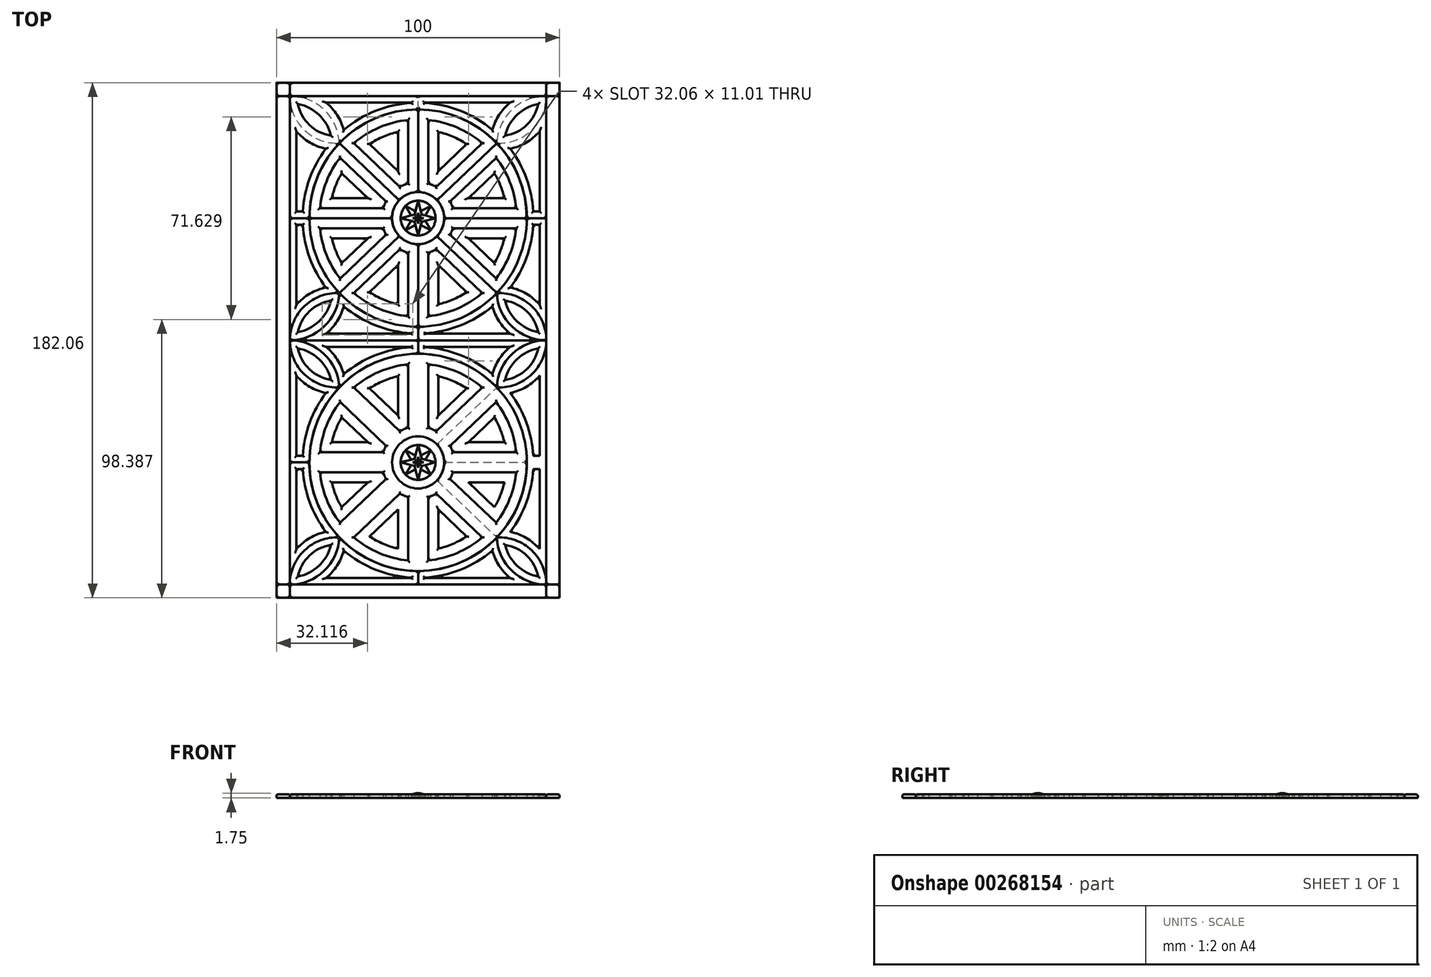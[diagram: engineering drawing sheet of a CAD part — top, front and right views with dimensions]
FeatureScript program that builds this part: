
annotation { "Feature Type Name" : "Feature", "Feature Type Description" : "" }
export const myFeature = defineFeature(function(context is Context, id is Id, definition is map)
    precondition{}
    {
        {
            var Q0;
            Q0=qCreatedBy(makeId("Top.planeOp"),FACE);
            var sketch = newSketch(context, id + "F0", { "sketchPlane" : qUnion([Q0])});
            skLineSegment(sketch, "E0", {"start": v(-100, 182.06) * mm, "end": v(-95.31, 182.06) * mm});
            skLineSegment(sketch, "E1", {"start": v(0, 182.06) * mm, "end": v(-4.69, 182.06) * mm});
            skLineSegment(sketch, "E2", {"start": v(0, 0) * mm, "end": v(-4.69, 0) * mm});
            skLineSegment(sketch, "E3", {"start": v(-100, 0) * mm, "end": v(-95.31, 0) * mm});
            skLineSegment(sketch, "E4", {"start": v(-100, 182.06) * mm, "end": v(-100, 177.37) * mm});
            skLineSegment(sketch, "E5", {"start": v(-100, 0) * mm, "end": v(-100, 4.69) * mm});
            skLineSegment(sketch, "E6", {"start": v(-95.31, 91.03) * mm, "end": v(-4.69, 91.03) * mm});
            skLineSegment(sketch, "E7", {"start": v(-56.66, 127.86) * mm, "end": v(-77.8, 107.7) * mm});
            skLineSegment(sketch, "E8", {"start": v(-56.66, 140.55) * mm, "end": v(-77.8, 160.7) * mm});
            skLineSegment(sketch, "E9", {"start": v(-50, 143.4) * mm, "end": v(-50, 172.61) * mm});
            skLineSegment(sketch, "E10", {"start": v(-50, 125) * mm, "end": v(-50, 95.8) * mm});
            skLineSegment(sketch, "E11", {"start": v(-40.8, 134.2) * mm, "end": v(-11.59, 134.2) * mm});
            skLineSegment(sketch, "E12", {"start": v(-59.2, 134.2) * mm, "end": v(-88.41, 134.2) * mm});
            skLineSegment(sketch, "E13", {"start": v(-43.34, 140.55) * mm, "end": v(-22.2, 160.7) * mm});
            skLineSegment(sketch, "E14", {"start": v(-43.34, 127.86) * mm, "end": v(-22.2, 107.7) * mm});
            skCircle(sketch, "E15.0", {"center": v(-50, 134.2) * mm, "radius": 6.15 * mm});
            skLineSegment(sketch, "E16", {"start": v(-11.59, 134.2) * mm, "end": v(-4.69, 134.2) * mm});
            skLineSegment(sketch, "E17", {"start": v(-88.41, 134.2) * mm, "end": v(-95.31, 134.2) * mm});
            skLineSegment(sketch, "E18", {"start": v(-50, 172.61) * mm, "end": v(-50, 177.37) * mm});
            skLineSegment(sketch, "E19", {"start": v(-50, 95.8) * mm, "end": v(-50, 91.03) * mm});
            skLineSegment(sketch, "E20", {"start": v(-56.15, 134.2) * mm, "end": v(-51.27, 135.47) * mm});
            skLineSegment(sketch, "E21", {"start": v(-50, 140.35) * mm, "end": v(-51.27, 135.47) * mm});
            skLineSegment(sketch, "E22", {"start": v(-50, 140.35) * mm, "end": v(-48.73, 135.46) * mm});
            skLineSegment(sketch, "E23", {"start": v(-43.85, 134.2) * mm, "end": v(-48.73, 135.46) * mm});
            skLineSegment(sketch, "E24", {"start": v(-43.85, 134.2) * mm, "end": v(-48.73, 132.93) * mm});
            skLineSegment(sketch, "E25", {"start": v(-50, 128.05) * mm, "end": v(-48.73, 132.93) * mm});
            skLineSegment(sketch, "E26", {"start": v(-50, 128.05) * mm, "end": v(-51.27, 132.93) * mm});
            skLineSegment(sketch, "E27", {"start": v(-56.15, 134.2) * mm, "end": v(-51.27, 132.93) * mm});
            skLineSegment(sketch, "E28", {"start": v(-45.55, 138.45) * mm, "end": v(-47.46, 135.13) * mm});
            skLineSegment(sketch, "E29", {"start": v(-45.55, 138.45) * mm, "end": v(-49.03, 136.63) * mm});
            skLineSegment(sketch, "E30", {"start": v(-54.45, 138.45) * mm, "end": v(-52.55, 135.14) * mm});
            skLineSegment(sketch, "E31", {"start": v(-54.45, 138.45) * mm, "end": v(-50.97, 136.63) * mm});
            skLineSegment(sketch, "E32", {"start": v(-54.45, 129.96) * mm, "end": v(-52.55, 133.26) * mm});
            skLineSegment(sketch, "E33", {"start": v(-54.45, 129.96) * mm, "end": v(-50.97, 131.77) * mm});
            skLineSegment(sketch, "E34", {"start": v(-45.55, 129.96) * mm, "end": v(-49.03, 131.77) * mm});
            skLineSegment(sketch, "E35", {"start": v(-45.55, 129.96) * mm, "end": v(-47.46, 133.26) * mm});
            skLineSegment(sketch, "E36.0", {"start": v(-50, 136.11) * mm, "end": v(-49.6, 134.59) * mm});
            skLineSegment(sketch, "E36.1", {"start": v(-48.1, 134.2) * mm, "end": v(-49.6, 134.59) * mm});
            skLineSegment(sketch, "E36.2", {"start": v(-50, 136.11) * mm, "end": v(-50.4, 134.6) * mm});
            skLineSegment(sketch, "E36.3", {"start": v(-48.1, 134.2) * mm, "end": v(-49.6, 133.8) * mm});
            skLineSegment(sketch, "E36.4", {"start": v(-51.91, 134.2) * mm, "end": v(-50.4, 134.6) * mm});
            skLineSegment(sketch, "E36.5", {"start": v(-51.91, 134.2) * mm, "end": v(-50.4, 133.8) * mm});
            skLineSegment(sketch, "E36.6", {"start": v(-50, 132.29) * mm, "end": v(-50.4, 133.8) * mm});
            skLineSegment(sketch, "E36.7", {"start": v(-50, 132.29) * mm, "end": v(-49.6, 133.8) * mm});
            skLineSegment(sketch, "E37", {"start": v(-95.31, 4.69) * mm, "end": v(-100, 4.69) * mm});
            skLineSegment(sketch, "E38", {"start": v(-95.31, 4.69) * mm, "end": v(-95.31, 0) * mm});
            skLineSegment(sketch, "E39", {"start": v(-95.31, 0) * mm, "end": v(-100, 0) * mm});
            skLineSegment(sketch, "E40", {"start": v(-100, 4.69) * mm, "end": v(-100, 0) * mm});
            skLineSegment(sketch, "E41", {"start": v(-4.69, 4.69) * mm, "end": v(0, 4.69) * mm});
            skLineSegment(sketch, "E42", {"start": v(0, 0) * mm, "end": v(0, 4.69) * mm});
            skLineSegment(sketch, "E43", {"start": v(-4.69, 0) * mm, "end": v(-4.69, 4.69) * mm});
            skLineSegment(sketch, "E44", {"start": v(-95.31, 0) * mm, "end": v(-4.69, 0) * mm});
            skLineSegment(sketch, "E45", {"start": v(-95.31, 4.69) * mm, "end": v(-4.69, 4.69) * mm});
            skLineSegment(sketch, "E46", {"start": v(-95.31, 177.37) * mm, "end": v(-100, 177.37) * mm});
            skLineSegment(sketch, "E47", {"start": v(-100, 177.37) * mm, "end": v(-100, 182.06) * mm});
            skLineSegment(sketch, "E48", {"start": v(-95.31, 182.06) * mm, "end": v(-95.31, 177.37) * mm});
            skLineSegment(sketch, "E49", {"start": v(-4.69, 177.37) * mm, "end": v(-4.69, 182.06) * mm});
            skLineSegment(sketch, "E50", {"start": v(0, 182.06) * mm, "end": v(0, 177.37) * mm});
            skLineSegment(sketch, "E51", {"start": v(0, 177.37) * mm, "end": v(-4.69, 177.37) * mm});
            skLineSegment(sketch, "E52", {"start": v(-100, 177.37) * mm, "end": v(-100, 4.69) * mm});
            skLineSegment(sketch, "E53", {"start": v(-4.69, 4.69) * mm, "end": v(-4.69, 177.37) * mm});
            skLineSegment(sketch, "E54", {"start": v(0, 4.69) * mm, "end": v(0, 177.37) * mm});
            skLineSegment(sketch, "E55", {"start": v(-4.69, 182.06) * mm, "end": v(-95.31, 182.06) * mm});
            skArc(sketch, "E56", {"start": v(-43.34, 127.86) * mm, "mid": v(-41.46, 130.78) * mm, "end": v(-40.8, 134.2) * mm});
            skArc(sketch, "E57", {"start": v(-50, 125) * mm, "mid": v(-46.38, 125.74) * mm, "end": v(-43.34, 127.86) * mm});
            skArc(sketch, "E58", {"start": v(-56.66, 127.86) * mm, "mid": v(-53.62, 125.74) * mm, "end": v(-50, 125) * mm});
            skArc(sketch, "E59", {"start": v(-59.2, 134.2) * mm, "mid": v(-58.54, 130.78) * mm, "end": v(-56.66, 127.86) * mm});
            skArc(sketch, "E60", {"start": v(-56.66, 140.55) * mm, "mid": v(-58.54, 137.62) * mm, "end": v(-59.2, 134.2) * mm});
            skArc(sketch, "E61", {"start": v(-50, 143.4) * mm, "mid": v(-53.62, 142.66) * mm, "end": v(-56.66, 140.55) * mm});
            skArc(sketch, "E62", {"start": v(-43.34, 140.55) * mm, "mid": v(-46.38, 142.66) * mm, "end": v(-50, 143.4) * mm});
            skArc(sketch, "E63", {"start": v(-40.8, 134.2) * mm, "mid": v(-41.46, 137.62) * mm, "end": v(-43.34, 140.55) * mm});
            skArc(sketch, "E64", {"start": v(-50, 95.8) * mm, "mid": v(-34.87, 98.9) * mm, "end": v(-22.2, 107.7) * mm});
            skArc(sketch, "E65", {"start": v(-77.8, 107.7) * mm, "mid": v(-65.13, 98.9) * mm, "end": v(-50, 95.8) * mm});
            skArc(sketch, "E66", {"start": v(-88.41, 134.2) * mm, "mid": v(-85.66, 119.93) * mm, "end": v(-77.8, 107.7) * mm});
            skArc(sketch, "E67", {"start": v(-77.8, 160.7) * mm, "mid": v(-85.66, 148.47) * mm, "end": v(-88.41, 134.2) * mm});
            skArc(sketch, "E68", {"start": v(-50, 172.61) * mm, "mid": v(-65.13, 169.5) * mm, "end": v(-77.8, 160.7) * mm});
            skArc(sketch, "E69", {"start": v(-22.2, 160.7) * mm, "mid": v(-34.87, 169.5) * mm, "end": v(-50, 172.61) * mm});
            skArc(sketch, "E70", {"start": v(-11.59, 134.2) * mm, "mid": v(-14.34, 148.47) * mm, "end": v(-22.2, 160.7) * mm});
            skArc(sketch, "E71", {"start": v(-22.2, 107.7) * mm, "mid": v(-14.34, 119.93) * mm, "end": v(-11.59, 134.2) * mm});
            skLineSegment(sketch, "E72.0", {"start": v(-56.42, 145.23) * mm, "end": v(-72.65, 160.7) * mm});
            skArc(sketch, "E72.1", {"start": v(-53.56, 146.45) * mm, "mid": v(-55.02, 145.93) * mm, "end": v(-56.42, 145.23) * mm});
            skLineSegment(sketch, "E72.2", {"start": v(-53.56, 146.45) * mm, "end": v(-53.56, 168.87) * mm});
            skArc(sketch, "E72.3", {"start": v(-53.56, 168.87) * mm, "mid": v(-63.73, 166.24) * mm, "end": v(-72.65, 160.7) * mm});
            skLineSegment(sketch, "E73.0", {"start": v(-57.11, 150.8) * mm, "end": v(-67.16, 160.38) * mm});
            skLineSegment(sketch, "E73.1", {"start": v(-57.11, 150.8) * mm, "end": v(-57.11, 164.68) * mm});
            skArc(sketch, "E73.2", {"start": v(-57.11, 164.68) * mm, "mid": v(-62.33, 162.97) * mm, "end": v(-67.16, 160.38) * mm});
            skArc(sketch, "E74.0", {"start": v(-77.56, 155.54) * mm, "mid": v(-82.36, 147.15) * mm, "end": v(-84.67, 137.76) * mm});
            skLineSegment(sketch, "E74.1", {"start": v(-61.32, 140.08) * mm, "end": v(-77.56, 155.54) * mm});
            skArc(sketch, "E74.2", {"start": v(-61.32, 140.08) * mm, "mid": v(-61.84, 138.94) * mm, "end": v(-62.25, 137.76) * mm});
            skLineSegment(sketch, "E74.3", {"start": v(-62.25, 137.76) * mm, "end": v(-84.67, 137.76) * mm});
            skArc(sketch, "E75.0", {"start": v(-76.97, 150.08) * mm, "mid": v(-79.06, 145.83) * mm, "end": v(-80.48, 141.31) * mm});
            skLineSegment(sketch, "E75.1", {"start": v(-67.78, 141.31) * mm, "end": v(-76.97, 150.08) * mm});
            skLineSegment(sketch, "E75.2", {"start": v(-67.78, 141.31) * mm, "end": v(-80.48, 141.31) * mm});
            skArc(sketch, "E76.0", {"start": v(-84.67, 130.65) * mm, "mid": v(-82.36, 121.25) * mm, "end": v(-77.56, 112.86) * mm});
            skLineSegment(sketch, "E76.1", {"start": v(-62.25, 130.65) * mm, "end": v(-84.67, 130.65) * mm});
            skArc(sketch, "E76.2", {"start": v(-62.25, 130.65) * mm, "mid": v(-61.84, 129.46) * mm, "end": v(-61.32, 128.33) * mm});
            skLineSegment(sketch, "E76.3", {"start": v(-61.32, 128.33) * mm, "end": v(-77.56, 112.86) * mm});
            skArc(sketch, "E77.0", {"start": v(-80.48, 127.09) * mm, "mid": v(-79.06, 122.57) * mm, "end": v(-76.97, 118.33) * mm});
            skLineSegment(sketch, "E77.1", {"start": v(-67.78, 127.09) * mm, "end": v(-80.48, 127.09) * mm});
            skLineSegment(sketch, "E77.2", {"start": v(-67.78, 127.09) * mm, "end": v(-76.97, 118.33) * mm});
            skArc(sketch, "E78.0", {"start": v(-72.65, 107.71) * mm, "mid": v(-63.73, 102.16) * mm, "end": v(-53.56, 99.53) * mm});
            skLineSegment(sketch, "E78.1", {"start": v(-56.42, 123.18) * mm, "end": v(-72.65, 107.71) * mm});
            skArc(sketch, "E78.2", {"start": v(-56.42, 123.18) * mm, "mid": v(-55.02, 122.48) * mm, "end": v(-53.56, 121.95) * mm});
            skLineSegment(sketch, "E78.3", {"start": v(-53.56, 121.95) * mm, "end": v(-53.56, 99.53) * mm});
            skArc(sketch, "E79.0", {"start": v(-67.16, 108.03) * mm, "mid": v(-62.33, 105.43) * mm, "end": v(-57.11, 103.72) * mm});
            skLineSegment(sketch, "E79.1", {"start": v(-57.11, 117.6) * mm, "end": v(-67.16, 108.03) * mm});
            skLineSegment(sketch, "E79.2", {"start": v(-57.11, 117.6) * mm, "end": v(-57.11, 103.72) * mm});
            skArc(sketch, "E80.0", {"start": v(-46.44, 99.53) * mm, "mid": v(-36.27, 102.16) * mm, "end": v(-27.35, 107.71) * mm});
            skLineSegment(sketch, "E80.1", {"start": v(-46.44, 121.95) * mm, "end": v(-46.44, 99.53) * mm});
            skArc(sketch, "E80.2", {"start": v(-46.44, 121.95) * mm, "mid": v(-44.98, 122.48) * mm, "end": v(-43.58, 123.18) * mm});
            skLineSegment(sketch, "E80.3", {"start": v(-43.58, 123.18) * mm, "end": v(-27.35, 107.71) * mm});
            skArc(sketch, "E81.0", {"start": v(-42.89, 103.72) * mm, "mid": v(-37.67, 105.43) * mm, "end": v(-32.84, 108.03) * mm});
            skLineSegment(sketch, "E81.1", {"start": v(-42.89, 117.6) * mm, "end": v(-42.89, 103.72) * mm});
            skLineSegment(sketch, "E81.2", {"start": v(-42.89, 117.6) * mm, "end": v(-32.84, 108.03) * mm});
            skArc(sketch, "E82.0", {"start": v(-27.35, 160.7) * mm, "mid": v(-36.27, 166.24) * mm, "end": v(-46.44, 168.87) * mm});
            skLineSegment(sketch, "E82.1", {"start": v(-43.58, 145.23) * mm, "end": v(-27.35, 160.7) * mm});
            skArc(sketch, "E82.2", {"start": v(-43.58, 145.23) * mm, "mid": v(-44.98, 145.93) * mm, "end": v(-46.44, 146.45) * mm});
            skLineSegment(sketch, "E82.3", {"start": v(-46.44, 146.45) * mm, "end": v(-46.44, 168.87) * mm});
            skLineSegment(sketch, "E83.0", {"start": v(-42.89, 150.8) * mm, "end": v(-32.84, 160.38) * mm});
            skLineSegment(sketch, "E83.1", {"start": v(-42.89, 150.8) * mm, "end": v(-42.89, 164.68) * mm});
            skArc(sketch, "E83.2", {"start": v(-32.84, 160.38) * mm, "mid": v(-37.67, 162.97) * mm, "end": v(-42.89, 164.68) * mm});
            skArc(sketch, "E84.0", {"start": v(-15.33, 137.76) * mm, "mid": v(-17.64, 147.15) * mm, "end": v(-22.44, 155.54) * mm});
            skLineSegment(sketch, "E84.1", {"start": v(-37.75, 137.76) * mm, "end": v(-15.33, 137.76) * mm});
            skArc(sketch, "E84.2", {"start": v(-37.75, 137.76) * mm, "mid": v(-38.16, 138.94) * mm, "end": v(-38.68, 140.08) * mm});
            skLineSegment(sketch, "E84.3", {"start": v(-38.68, 140.08) * mm, "end": v(-22.44, 155.54) * mm});
            skLineSegment(sketch, "E85.0", {"start": v(-32.22, 141.31) * mm, "end": v(-23.03, 150.08) * mm});
            skLineSegment(sketch, "E85.1", {"start": v(-32.22, 141.31) * mm, "end": v(-19.52, 141.31) * mm});
            skArc(sketch, "E85.2", {"start": v(-19.52, 141.31) * mm, "mid": v(-20.94, 145.83) * mm, "end": v(-23.03, 150.08) * mm});
            skArc(sketch, "E86.0", {"start": v(-22.44, 112.86) * mm, "mid": v(-17.64, 121.25) * mm, "end": v(-15.33, 130.65) * mm});
            skLineSegment(sketch, "E86.1", {"start": v(-38.68, 128.33) * mm, "end": v(-22.44, 112.86) * mm});
            skArc(sketch, "E86.2", {"start": v(-38.68, 128.33) * mm, "mid": v(-38.16, 129.46) * mm, "end": v(-37.75, 130.65) * mm});
            skLineSegment(sketch, "E86.3", {"start": v(-37.75, 130.65) * mm, "end": v(-15.33, 130.65) * mm});
            skArc(sketch, "E87.0", {"start": v(-23.03, 118.33) * mm, "mid": v(-20.94, 122.57) * mm, "end": v(-19.52, 127.09) * mm});
            skLineSegment(sketch, "E87.1", {"start": v(-32.22, 127.09) * mm, "end": v(-23.03, 118.33) * mm});
            skLineSegment(sketch, "E87.2", {"start": v(-32.22, 127.09) * mm, "end": v(-19.52, 127.09) * mm});
            skLineSegment(sketch, "E88.MirrorCS", {"start": v(-48.1, 47.86) * mm, "end": v(-49.6, 47.47) * mm});
            skLineSegment(sketch, "E89.MirrorCS", {"start": v(-50, 49.77) * mm, "end": v(-50.4, 48.25) * mm});
            skLineSegment(sketch, "E90.MirrorCS", {"start": v(-51.91, 47.86) * mm, "end": v(-50.4, 48.25) * mm});
            skLineSegment(sketch, "E91.MirrorCS", {"start": v(-48.1, 47.86) * mm, "end": v(-49.6, 48.25) * mm});
            skLineSegment(sketch, "E92.MirrorCS", {"start": v(-50, 45.95) * mm, "end": v(-50.4, 47.46) * mm});
            skLineSegment(sketch, "E93.MirrorCS", {"start": v(-50, 45.95) * mm, "end": v(-49.6, 47.47) * mm});
            skLineSegment(sketch, "E94.MirrorCS", {"start": v(-50, 49.77) * mm, "end": v(-49.6, 48.25) * mm});
            skLineSegment(sketch, "E95.MirrorCS", {"start": v(-51.91, 47.86) * mm, "end": v(-50.4, 47.46) * mm});
            skLineSegment(sketch, "E96.MirrorCS", {"start": v(-56.15, 47.86) * mm, "end": v(-51.27, 46.59) * mm});
            skLineSegment(sketch, "E97.MirrorCS", {"start": v(-50, 86.27) * mm, "end": v(-50, 91.03) * mm});
            skLineSegment(sketch, "E98.MirrorCS", {"start": v(-50, 9.45) * mm, "end": v(-50, 4.69) * mm});
            skLineSegment(sketch, "E99.MirrorCS", {"start": v(-56.15, 47.86) * mm, "end": v(-51.27, 49.13) * mm});
            skLineSegment(sketch, "E100.MirrorCS", {"start": v(-50, 41.7) * mm, "end": v(-51.27, 46.59) * mm});
            skLineSegment(sketch, "E101.MirrorCS", {"start": v(-43.85, 47.86) * mm, "end": v(-48.73, 46.6) * mm});
            skLineSegment(sketch, "E102.MirrorCS", {"start": v(-54.45, 43.61) * mm, "end": v(-52.55, 46.92) * mm});
            skLineSegment(sketch, "E103.MirrorCS", {"start": v(-45.55, 43.61) * mm, "end": v(-47.46, 46.93) * mm});
            skLineSegment(sketch, "E104.MirrorCS", {"start": v(-50, 41.7) * mm, "end": v(-48.73, 46.6) * mm});
            skArc(sketch, "E105.MirrorCS", {"start": v(-43.34, 54.2) * mm, "mid": v(-41.46, 51.28) * mm, "end": v(-40.8, 47.86) * mm});
            skLineSegment(sketch, "E106.MirrorCS", {"start": v(-45.55, 52.1) * mm, "end": v(-47.46, 48.8) * mm});
            skLineSegment(sketch, "E107.MirrorCS", {"start": v(-45.55, 52.1) * mm, "end": v(-49.03, 50.3) * mm});
            skArc(sketch, "E108.MirrorCS", {"start": v(-56.66, 54.2) * mm, "mid": v(-53.62, 56.31) * mm, "end": v(-50, 57.06) * mm});
            skArc(sketch, "E109.MirrorCS", {"start": v(-56.66, 41.51) * mm, "mid": v(-58.54, 44.44) * mm, "end": v(-59.2, 47.86) * mm});
            skLineSegment(sketch, "E110.MirrorCS", {"start": v(-43.85, 47.86) * mm, "end": v(-48.73, 49.13) * mm});
            skLineSegment(sketch, "E111.MirrorCS", {"start": v(-50, 54.01) * mm, "end": v(-48.73, 49.13) * mm});
            skArc(sketch, "E112.MirrorCS", {"start": v(-40.8, 47.86) * mm, "mid": v(-41.46, 44.44) * mm, "end": v(-43.34, 41.51) * mm});
            skArc(sketch, "E113.MirrorCS", {"start": v(-50, 38.66) * mm, "mid": v(-53.62, 39.4) * mm, "end": v(-56.66, 41.51) * mm});
            skArc(sketch, "E114.MirrorCS", {"start": v(-59.2, 47.86) * mm, "mid": v(-58.54, 51.28) * mm, "end": v(-56.66, 54.2) * mm});
            skLineSegment(sketch, "E115.MirrorCS", {"start": v(-54.45, 43.61) * mm, "end": v(-50.97, 45.43) * mm});
            skLineSegment(sketch, "E116.MirrorCS", {"start": v(-54.45, 52.1) * mm, "end": v(-50.97, 50.3) * mm});
            skLineSegment(sketch, "E117.MirrorCS", {"start": v(-45.55, 43.61) * mm, "end": v(-49.03, 45.43) * mm});
            skLineSegment(sketch, "E118.MirrorCS", {"start": v(-50, 54.01) * mm, "end": v(-51.27, 49.13) * mm});
            skLineSegment(sketch, "E119.MirrorCS", {"start": v(-54.45, 52.1) * mm, "end": v(-52.55, 48.8) * mm});
            skArc(sketch, "E120.MirrorCS", {"start": v(-62.25, 51.41) * mm, "mid": v(-61.84, 52.6) * mm, "end": v(-61.32, 53.73) * mm});
            skArc(sketch, "E121.MirrorCS", {"start": v(-61.32, 41.98) * mm, "mid": v(-61.84, 43.12) * mm, "end": v(-62.25, 44.3) * mm});
            skCircle(sketch, "E122.MirrorC", {"center": v(-50, 47.86) * mm, "radius": 6.15 * mm});
            skArc(sketch, "E123.MirrorCS", {"start": v(-53.56, 35.6) * mm, "mid": v(-55.02, 36.13) * mm, "end": v(-56.42, 36.83) * mm});
            skArc(sketch, "E124.MirrorCS", {"start": v(-43.58, 36.83) * mm, "mid": v(-44.98, 36.13) * mm, "end": v(-46.44, 35.6) * mm});
            skArc(sketch, "E125.MirrorCS", {"start": v(-56.42, 58.88) * mm, "mid": v(-55.02, 59.58) * mm, "end": v(-53.56, 60.1) * mm});
            skArc(sketch, "E126.MirrorCS", {"start": v(-38.68, 53.73) * mm, "mid": v(-38.16, 52.6) * mm, "end": v(-37.75, 51.41) * mm});
            skArc(sketch, "E127.MirrorCS", {"start": v(-37.75, 44.3) * mm, "mid": v(-38.16, 43.12) * mm, "end": v(-38.68, 41.98) * mm});
            skArc(sketch, "E128.MirrorCS", {"start": v(-46.44, 60.1) * mm, "mid": v(-44.98, 59.58) * mm, "end": v(-43.58, 58.88) * mm});
            skArc(sketch, "E129.MirrorCS", {"start": v(-42.89, 78.34) * mm, "mid": v(-37.67, 76.63) * mm, "end": v(-32.84, 74.03) * mm});
            skArc(sketch, "E130.MirrorCS", {"start": v(-67.16, 74.03) * mm, "mid": v(-62.33, 76.63) * mm, "end": v(-57.11, 78.34) * mm});
            skLineSegment(sketch, "E131.MirrorCS", {"start": v(-32.22, 40.75) * mm, "end": v(-23.03, 31.98) * mm});
            skArc(sketch, "E132.MirrorCS", {"start": v(-23.03, 63.73) * mm, "mid": v(-20.94, 59.48) * mm, "end": v(-19.52, 54.97) * mm});
            skArc(sketch, "E133.MirrorCS", {"start": v(-76.97, 31.98) * mm, "mid": v(-79.06, 36.23) * mm, "end": v(-80.48, 40.75) * mm});
            skArc(sketch, "E134.MirrorCS", {"start": v(-80.48, 54.97) * mm, "mid": v(-79.06, 59.48) * mm, "end": v(-76.97, 63.73) * mm});
            skArc(sketch, "E135.MirrorCS", {"start": v(-19.52, 40.75) * mm, "mid": v(-20.94, 36.23) * mm, "end": v(-23.03, 31.98) * mm});
            skLineSegment(sketch, "E136.MirrorCS", {"start": v(-56.42, 36.83) * mm, "end": v(-72.65, 21.37) * mm});
            skArc(sketch, "E137.MirrorCS", {"start": v(-72.65, 74.35) * mm, "mid": v(-63.73, 79.9) * mm, "end": v(-53.56, 82.53) * mm});
            skLineSegment(sketch, "E138.MirrorCS", {"start": v(-32.22, 54.97) * mm, "end": v(-23.03, 63.73) * mm});
            skLineSegment(sketch, "E139.MirrorCS", {"start": v(-46.44, 35.6) * mm, "end": v(-46.44, 13.19) * mm});
            skLineSegment(sketch, "E140.MirrorCS", {"start": v(-62.25, 51.41) * mm, "end": v(-84.67, 51.41) * mm});
            skArc(sketch, "E141.MirrorCS", {"start": v(-22.2, 74.35) * mm, "mid": v(-14.34, 62.13) * mm, "end": v(-11.59, 47.86) * mm});
            skLineSegment(sketch, "E142.MirrorCS", {"start": v(-32.22, 40.75) * mm, "end": v(-19.52, 40.75) * mm});
            skLineSegment(sketch, "E143.MirrorCS", {"start": v(-43.58, 58.88) * mm, "end": v(-27.35, 74.35) * mm});
            skLineSegment(sketch, "E144.MirrorCS", {"start": v(-42.89, 31.26) * mm, "end": v(-42.89, 17.38) * mm});
            skArc(sketch, "E145.MirrorCS", {"start": v(-15.33, 44.3) * mm, "mid": v(-17.64, 34.91) * mm, "end": v(-22.44, 26.52) * mm});
            skLineSegment(sketch, "E146.MirrorCS", {"start": v(-57.11, 64.46) * mm, "end": v(-67.16, 74.03) * mm});
            skLineSegment(sketch, "E147.MirrorCS", {"start": v(-61.32, 41.98) * mm, "end": v(-77.56, 26.52) * mm});
            skArc(sketch, "E148.MirrorCS", {"start": v(-50, 86.27) * mm, "mid": v(-34.87, 83.16) * mm, "end": v(-22.2, 74.35) * mm});
            skLineSegment(sketch, "E149.MirrorCS", {"start": v(-53.56, 35.6) * mm, "end": v(-53.56, 13.19) * mm});
            skLineSegment(sketch, "E150.MirrorCS", {"start": v(-38.68, 53.73) * mm, "end": v(-22.44, 69.2) * mm});
            skArc(sketch, "E151.MirrorCS", {"start": v(-43.34, 41.51) * mm, "mid": v(-46.38, 39.4) * mm, "end": v(-50, 38.66) * mm});
            skLineSegment(sketch, "E152.MirrorCS", {"start": v(-56.42, 58.88) * mm, "end": v(-72.65, 74.35) * mm});
            skArc(sketch, "E153.MirrorCS", {"start": v(-77.8, 74.35) * mm, "mid": v(-65.13, 83.16) * mm, "end": v(-50, 86.27) * mm});
            skLineSegment(sketch, "E154.MirrorCS", {"start": v(-57.11, 31.26) * mm, "end": v(-57.11, 17.38) * mm});
            skLineSegment(sketch, "E155.MirrorCS", {"start": v(-53.56, 60.1) * mm, "end": v(-53.56, 82.53) * mm});
            skLineSegment(sketch, "E156.MirrorCS", {"start": v(-62.25, 44.3) * mm, "end": v(-84.67, 44.3) * mm});
            skArc(sketch, "E157.MirrorCS", {"start": v(-27.35, 21.37) * mm, "mid": v(-36.27, 15.82) * mm, "end": v(-46.44, 13.19) * mm});
            skArc(sketch, "E158.MirrorCS", {"start": v(-77.56, 26.52) * mm, "mid": v(-82.36, 34.91) * mm, "end": v(-84.67, 44.3) * mm});
            skLineSegment(sketch, "E159.MirrorCS", {"start": v(-67.78, 54.97) * mm, "end": v(-76.97, 63.73) * mm});
            skLineSegment(sketch, "E160.MirrorCS", {"start": v(-42.89, 64.46) * mm, "end": v(-32.84, 74.03) * mm});
            skLineSegment(sketch, "E161.MirrorCS", {"start": v(-57.11, 64.46) * mm, "end": v(-57.11, 78.34) * mm});
            skLineSegment(sketch, "E162.MirrorCS", {"start": v(-61.32, 53.73) * mm, "end": v(-77.56, 69.2) * mm});
            skLineSegment(sketch, "E163.MirrorCS", {"start": v(-37.75, 44.3) * mm, "end": v(-15.33, 44.3) * mm});
            skLineSegment(sketch, "E164.MirrorCS", {"start": v(-42.89, 64.46) * mm, "end": v(-42.89, 78.34) * mm});
            skLineSegment(sketch, "E165.MirrorCS", {"start": v(-67.78, 54.97) * mm, "end": v(-80.48, 54.97) * mm});
            skLineSegment(sketch, "E166.MirrorCS", {"start": v(-46.44, 60.1) * mm, "end": v(-46.44, 82.53) * mm});
            skArc(sketch, "E167.MirrorCS", {"start": v(-22.2, 21.36) * mm, "mid": v(-34.87, 12.55) * mm, "end": v(-50, 9.45) * mm});
            skArc(sketch, "E168.MirrorCS", {"start": v(-22.44, 69.2) * mm, "mid": v(-17.64, 60.8) * mm, "end": v(-15.33, 51.41) * mm});
            skArc(sketch, "E169.MirrorCS", {"start": v(-32.84, 21.68) * mm, "mid": v(-37.67, 19.09) * mm, "end": v(-42.89, 17.38) * mm});
            skLineSegment(sketch, "E170.MirrorCS", {"start": v(-88.41, 47.86) * mm, "end": v(-95.31, 47.86) * mm});
            skLineSegment(sketch, "E171.MirrorCS", {"start": v(-43.34, 41.51) * mm, "end": v(-22.2, 21.36) * mm});
            skArc(sketch, "E172.MirrorCS", {"start": v(-46.44, 82.53) * mm, "mid": v(-36.27, 79.9) * mm, "end": v(-27.35, 74.35) * mm});
            skLineSegment(sketch, "E173.MirrorCS", {"start": v(-50, 38.66) * mm, "end": v(-50, 9.45) * mm});
            skArc(sketch, "E174.MirrorCS", {"start": v(-11.59, 47.86) * mm, "mid": v(-14.34, 33.59) * mm, "end": v(-22.2, 21.36) * mm});
            skLineSegment(sketch, "E175.MirrorCS", {"start": v(-57.11, 31.26) * mm, "end": v(-67.16, 21.68) * mm});
            skLineSegment(sketch, "E176.MirrorCS", {"start": v(-32.22, 54.97) * mm, "end": v(-19.52, 54.97) * mm});
            skLineSegment(sketch, "E177.MirrorCS", {"start": v(-38.68, 41.98) * mm, "end": v(-22.44, 26.52) * mm});
            skLineSegment(sketch, "E178.MirrorCS", {"start": v(-67.78, 40.75) * mm, "end": v(-80.48, 40.75) * mm});
            skLineSegment(sketch, "E179.MirrorCS", {"start": v(-42.89, 31.26) * mm, "end": v(-32.84, 21.68) * mm});
            skArc(sketch, "E180.MirrorCS", {"start": v(-77.8, 21.36) * mm, "mid": v(-85.66, 33.59) * mm, "end": v(-88.41, 47.86) * mm});
            skLineSegment(sketch, "E181.MirrorCS", {"start": v(-43.34, 54.2) * mm, "end": v(-22.2, 74.35) * mm});
            skLineSegment(sketch, "E182.MirrorCS", {"start": v(-11.59, 47.86) * mm, "end": v(-4.69, 47.86) * mm});
            skLineSegment(sketch, "E183.MirrorCS", {"start": v(-40.8, 47.86) * mm, "end": v(-11.59, 47.86) * mm});
            skArc(sketch, "E184.MirrorCS", {"start": v(-53.56, 13.19) * mm, "mid": v(-63.73, 15.82) * mm, "end": v(-72.65, 21.37) * mm});
            skArc(sketch, "E185.MirrorCS", {"start": v(-88.41, 47.86) * mm, "mid": v(-85.66, 62.13) * mm, "end": v(-77.8, 74.35) * mm});
            skLineSegment(sketch, "E186.MirrorCS", {"start": v(-56.66, 54.2) * mm, "end": v(-77.8, 74.35) * mm});
            skArc(sketch, "E187.MirrorCS", {"start": v(-57.11, 17.38) * mm, "mid": v(-62.33, 19.09) * mm, "end": v(-67.16, 21.68) * mm});
            skLineSegment(sketch, "E188.MirrorCS", {"start": v(-50, 57.06) * mm, "end": v(-50, 86.27) * mm});
            skArc(sketch, "E189.MirrorCS", {"start": v(-50, 9.45) * mm, "mid": v(-65.13, 12.55) * mm, "end": v(-77.8, 21.36) * mm});
            skLineSegment(sketch, "E190.MirrorCS", {"start": v(-67.78, 40.75) * mm, "end": v(-76.97, 31.98) * mm});
            skArc(sketch, "E191.MirrorCS", {"start": v(-50, 57.06) * mm, "mid": v(-46.38, 56.31) * mm, "end": v(-43.34, 54.2) * mm});
            skLineSegment(sketch, "E192.MirrorCS", {"start": v(-37.75, 51.41) * mm, "end": v(-15.33, 51.41) * mm});
            skLineSegment(sketch, "E193.MirrorCS", {"start": v(-43.58, 36.83) * mm, "end": v(-27.35, 21.37) * mm});
            skLineSegment(sketch, "E194.MirrorCS", {"start": v(-59.2, 47.86) * mm, "end": v(-88.41, 47.86) * mm});
            skArc(sketch, "E195.MirrorCS", {"start": v(-84.67, 51.41) * mm, "mid": v(-82.36, 60.8) * mm, "end": v(-77.56, 69.2) * mm});
            skLineSegment(sketch, "E196.MirrorCS", {"start": v(-56.66, 41.51) * mm, "end": v(-77.8, 21.36) * mm});
            skArc(sketch, "E197", {"start": v(-77.8, 74.35) * mm, "mid": v(-83.23, 86.2) * mm, "end": v(-95.31, 91.03) * mm});
            skArc(sketch, "E198", {"start": v(-95.31, 91.03) * mm, "mid": v(-90.12, 78.96) * mm, "end": v(-77.8, 74.35) * mm});
            skArc(sketch, "E199.MirrorCS", {"start": v(-77.8, 107.7) * mm, "mid": v(-83.23, 95.87) * mm, "end": v(-95.31, 91.03) * mm});
            skArc(sketch, "E200.MirrorCS", {"start": v(-95.31, 91.03) * mm, "mid": v(-90.12, 103.1) * mm, "end": v(-77.8, 107.7) * mm});
            skArc(sketch, "E201.MirrorCS", {"start": v(-4.69, 91.03) * mm, "mid": v(-9.88, 103.1) * mm, "end": v(-22.2, 107.7) * mm});
            skArc(sketch, "E202.MirrorCS", {"start": v(-22.2, 74.35) * mm, "mid": v(-16.77, 86.2) * mm, "end": v(-4.69, 91.03) * mm});
            skArc(sketch, "E203.MirrorCS", {"start": v(-4.69, 91.03) * mm, "mid": v(-9.88, 78.96) * mm, "end": v(-22.2, 74.35) * mm});
            skArc(sketch, "E204", {"start": v(-77.8, 21.36) * mm, "mid": v(-90.13, 16.77) * mm, "end": v(-95.31, 4.69) * mm});
            skArc(sketch, "E205", {"start": v(-95.31, 4.69) * mm, "mid": v(-83.23, 9.52) * mm, "end": v(-77.8, 21.36) * mm});
            skArc(sketch, "E206", {"start": v(-4.69, 4.69) * mm, "mid": v(-9.87, 16.77) * mm, "end": v(-22.2, 21.36) * mm});
            skArc(sketch, "E207", {"start": v(-22.2, 21.36) * mm, "mid": v(-16.77, 9.52) * mm, "end": v(-4.69, 4.69) * mm});
            skArc(sketch, "E208.MirrorCS", {"start": v(-4.69, 177.37) * mm, "mid": v(-9.87, 165.29) * mm, "end": v(-22.2, 160.7) * mm});
            skArc(sketch, "E209.MirrorCS", {"start": v(-22.2, 160.7) * mm, "mid": v(-16.77, 172.54) * mm, "end": v(-4.69, 177.37) * mm});
            skArc(sketch, "E210.MirrorCS", {"start": v(-95.31, 177.37) * mm, "mid": v(-83.23, 172.54) * mm, "end": v(-77.8, 160.7) * mm});
            skArc(sketch, "E211.MirrorCS", {"start": v(-77.8, 160.7) * mm, "mid": v(-90.13, 165.29) * mm, "end": v(-95.31, 177.37) * mm});
            skArc(sketch, "E212.0", {"start": v(-19.25, 163.38) * mm, "mid": v(-15.02, 170.7) * mm, "end": v(-7.5, 174.57) * mm});
            skArc(sketch, "E212.1", {"start": v(-7.5, 174.57) * mm, "mid": v(-11.62, 167.12) * mm, "end": v(-19.25, 163.38) * mm});
            skArc(sketch, "E213.0", {"start": v(-92.5, 174.57) * mm, "mid": v(-84.98, 170.7) * mm, "end": v(-80.75, 163.38) * mm});
            skArc(sketch, "E213.1", {"start": v(-80.75, 163.38) * mm, "mid": v(-88.38, 167.12) * mm, "end": v(-92.5, 174.57) * mm});
            skArc(sketch, "E214.0", {"start": v(-92.48, 93.84) * mm, "mid": v(-88.37, 101.26) * mm, "end": v(-80.75, 105.01) * mm});
            skArc(sketch, "E214.1", {"start": v(-80.75, 105.01) * mm, "mid": v(-84.98, 97.7) * mm, "end": v(-92.48, 93.84) * mm});
            skArc(sketch, "E215.0", {"start": v(-7.52, 93.84) * mm, "mid": v(-11.63, 101.26) * mm, "end": v(-19.25, 105.01) * mm});
            skArc(sketch, "E215.1", {"start": v(-19.25, 105.01) * mm, "mid": v(-15.02, 97.7) * mm, "end": v(-7.52, 93.84) * mm});
            skArc(sketch, "E216.MirrorCS", {"start": v(-19.25, 77.05) * mm, "mid": v(-15.02, 84.35) * mm, "end": v(-7.52, 88.22) * mm});
            skArc(sketch, "E217.MirrorCS", {"start": v(-7.52, 88.22) * mm, "mid": v(-11.63, 80.8) * mm, "end": v(-19.25, 77.05) * mm});
            skArc(sketch, "E218.MirrorCS", {"start": v(-7.5, 7.5) * mm, "mid": v(-11.62, 14.94) * mm, "end": v(-19.25, 18.68) * mm});
            skArc(sketch, "E219.MirrorCS", {"start": v(-19.25, 18.68) * mm, "mid": v(-15.02, 11.36) * mm, "end": v(-7.5, 7.5) * mm});
            skArc(sketch, "E220.MirrorCS", {"start": v(-80.75, 18.68) * mm, "mid": v(-88.38, 14.94) * mm, "end": v(-92.5, 7.5) * mm});
            skArc(sketch, "E221.MirrorCS", {"start": v(-92.5, 7.5) * mm, "mid": v(-84.98, 11.36) * mm, "end": v(-80.75, 18.68) * mm});
            skArc(sketch, "E222.MirrorCS", {"start": v(-92.48, 88.22) * mm, "mid": v(-88.37, 80.8) * mm, "end": v(-80.75, 77.05) * mm});
            skArc(sketch, "E223.MirrorCS", {"start": v(-80.75, 77.05) * mm, "mid": v(-84.98, 84.35) * mm, "end": v(-92.48, 88.22) * mm});
            skLineSegment(sketch, "E224", {"start": v(-95.31, 177.37) * mm, "end": v(-95.31, 134.2) * mm});
            skLineSegment(sketch, "E225", {"start": v(-95.31, 134.2) * mm, "end": v(-95.31, 91.03) * mm});
            skLineSegment(sketch, "E226", {"start": v(-95.31, 91.03) * mm, "end": v(-95.31, 47.86) * mm});
            skLineSegment(sketch, "E227", {"start": v(-95.31, 47.86) * mm, "end": v(-95.31, 4.69) * mm});
            skLineSegment(sketch, "E228", {"start": v(-4.69, 177.37) * mm, "end": v(-50, 177.37) * mm});
            skLineSegment(sketch, "E229", {"start": v(-50, 177.37) * mm, "end": v(-95.31, 177.37) * mm});
            skArc(sketch, "E230.0", {"start": v(-23.78, 165.42) * mm, "mid": v(-21.37, 170.67) * mm, "end": v(-17.55, 175.01) * mm});
            skArc(sketch, "E230.1", {"start": v(-23.78, 165.42) * mm, "mid": v(-34.94, 172.1) * mm, "end": v(-47.64, 174.9) * mm});
            skLineSegment(sketch, "E230.2", {"start": v(-47.64, 174.9) * mm, "end": v(-47.64, 175.01) * mm});
            skLineSegment(sketch, "E230.3", {"start": v(-17.55, 175.01) * mm, "end": v(-47.64, 175.01) * mm});
            skArc(sketch, "E231.MirrorCS", {"start": v(-76.22, 165.42) * mm, "mid": v(-65.06, 172.1) * mm, "end": v(-52.36, 174.9) * mm});
            skLineSegment(sketch, "E232.MirrorCS", {"start": v(-52.36, 174.9) * mm, "end": v(-52.36, 175.01) * mm});
            skLineSegment(sketch, "E233.MirrorCS", {"start": v(-82.45, 175.01) * mm, "end": v(-52.36, 175.01) * mm});
            skArc(sketch, "E234.MirrorCS", {"start": v(-76.22, 165.42) * mm, "mid": v(-78.63, 170.67) * mm, "end": v(-82.45, 175.01) * mm});
            skArc(sketch, "E235.MirrorCS", {"start": v(-76.22, 102.98) * mm, "mid": v(-65.06, 96.31) * mm, "end": v(-52.36, 93.5) * mm});
            skArc(sketch, "E236.MirrorCS", {"start": v(-76.22, 102.98) * mm, "mid": v(-78.63, 97.73) * mm, "end": v(-82.45, 93.4) * mm});
            skLineSegment(sketch, "E237.MirrorCS", {"start": v(-82.45, 93.4) * mm, "end": v(-52.36, 93.4) * mm});
            skLineSegment(sketch, "E238.MirrorCS", {"start": v(-52.36, 93.5) * mm, "end": v(-52.36, 93.4) * mm});
            skLineSegment(sketch, "E239.MirrorCS", {"start": v(-47.64, 93.5) * mm, "end": v(-47.64, 93.4) * mm});
            skLineSegment(sketch, "E240.MirrorCS", {"start": v(-17.55, 93.4) * mm, "end": v(-47.64, 93.4) * mm});
            skArc(sketch, "E241.MirrorCS", {"start": v(-23.78, 102.98) * mm, "mid": v(-34.94, 96.31) * mm, "end": v(-47.64, 93.5) * mm});
            skArc(sketch, "E242.MirrorCS", {"start": v(-23.78, 102.98) * mm, "mid": v(-21.37, 97.73) * mm, "end": v(-17.55, 93.4) * mm});
            skArc(sketch, "E243.MirrorCS", {"start": v(-23.78, 79.08) * mm, "mid": v(-34.94, 85.75) * mm, "end": v(-47.64, 88.56) * mm});
            skArc(sketch, "E244.MirrorCS", {"start": v(-23.78, 79.08) * mm, "mid": v(-21.37, 84.33) * mm, "end": v(-17.55, 88.67) * mm});
            skLineSegment(sketch, "E245.MirrorCS", {"start": v(-17.55, 88.67) * mm, "end": v(-47.64, 88.67) * mm});
            skLineSegment(sketch, "E246.MirrorCS", {"start": v(-47.64, 88.56) * mm, "end": v(-47.64, 88.67) * mm});
            skLineSegment(sketch, "E247.MirrorCS", {"start": v(-82.45, 88.67) * mm, "end": v(-52.36, 88.67) * mm});
            skArc(sketch, "E248.MirrorCS", {"start": v(-76.22, 79.08) * mm, "mid": v(-65.06, 85.75) * mm, "end": v(-52.36, 88.56) * mm});
            skArc(sketch, "E249.MirrorCS", {"start": v(-76.22, 79.08) * mm, "mid": v(-78.63, 84.33) * mm, "end": v(-82.45, 88.67) * mm});
            skLineSegment(sketch, "E250.MirrorCS", {"start": v(-52.36, 88.56) * mm, "end": v(-52.36, 88.67) * mm});
            skLineSegment(sketch, "E251.MirrorCS", {"start": v(-17.55, 7.05) * mm, "end": v(-47.64, 7.05) * mm});
            skArc(sketch, "E252.MirrorCS", {"start": v(-23.78, 16.64) * mm, "mid": v(-34.94, 9.97) * mm, "end": v(-47.64, 7.15) * mm});
            skLineSegment(sketch, "E253.MirrorCS", {"start": v(-47.64, 7.15) * mm, "end": v(-47.64, 7.05) * mm});
            skLineSegment(sketch, "E254.MirrorCS", {"start": v(-82.45, 7.05) * mm, "end": v(-52.36, 7.05) * mm});
            skArc(sketch, "E255.MirrorCS", {"start": v(-76.22, 16.64) * mm, "mid": v(-65.06, 9.97) * mm, "end": v(-52.36, 7.15) * mm});
            skLineSegment(sketch, "E256.MirrorCS", {"start": v(-52.36, 7.15) * mm, "end": v(-52.36, 7.05) * mm});
            skArc(sketch, "E257.MirrorCS", {"start": v(-76.22, 16.64) * mm, "mid": v(-78.63, 11.39) * mm, "end": v(-82.45, 7.05) * mm});
            skArc(sketch, "E258.MirrorCS", {"start": v(-23.78, 16.64) * mm, "mid": v(-21.37, 11.39) * mm, "end": v(-17.55, 7.05) * mm});
            skArc(sketch, "E259.0", {"start": v(-82.57, 158.73) * mm, "mid": v(-88.25, 160.93) * mm, "end": v(-92.95, 164.81) * mm});
            skArc(sketch, "E259.1", {"start": v(-82.57, 158.73) * mm, "mid": v(-88.28, 148.25) * mm, "end": v(-90.7, 136.56) * mm});
            skLineSegment(sketch, "E259.2", {"start": v(-90.7, 136.56) * mm, "end": v(-92.95, 136.56) * mm});
            skLineSegment(sketch, "E259.3", {"start": v(-92.95, 164.81) * mm, "end": v(-92.95, 136.56) * mm});
            skLineSegment(sketch, "E260.MirrorCS", {"start": v(-90.7, 131.84) * mm, "end": v(-92.95, 131.84) * mm});
            skArc(sketch, "E261.MirrorCS", {"start": v(-82.57, 109.67) * mm, "mid": v(-88.28, 120.15) * mm, "end": v(-90.7, 131.84) * mm});
            skArc(sketch, "E262.MirrorCS", {"start": v(-82.57, 109.67) * mm, "mid": v(-88.25, 107.47) * mm, "end": v(-92.95, 103.6) * mm});
            skLineSegment(sketch, "E263.MirrorCS", {"start": v(-92.95, 103.6) * mm, "end": v(-92.95, 131.84) * mm});
            skArc(sketch, "E264.MirrorCS", {"start": v(-17.43, 158.73) * mm, "mid": v(-11.72, 148.25) * mm, "end": v(-9.3, 136.56) * mm});
            skLineSegment(sketch, "E265.MirrorCS", {"start": v(-7.05, 164.81) * mm, "end": v(-7.05, 136.56) * mm});
            skLineSegment(sketch, "E266.MirrorCS", {"start": v(-9.3, 136.56) * mm, "end": v(-7.05, 136.56) * mm});
            skArc(sketch, "E267.MirrorCS", {"start": v(-17.43, 158.73) * mm, "mid": v(-11.75, 160.93) * mm, "end": v(-7.05, 164.81) * mm});
            skLineSegment(sketch, "E268.MirrorCS", {"start": v(-9.3, 131.84) * mm, "end": v(-7.05, 131.84) * mm});
            skArc(sketch, "E269.MirrorCS", {"start": v(-17.43, 109.67) * mm, "mid": v(-11.72, 120.15) * mm, "end": v(-9.3, 131.84) * mm});
            skLineSegment(sketch, "E270.MirrorCS", {"start": v(-7.05, 103.6) * mm, "end": v(-7.05, 131.84) * mm});
            skArc(sketch, "E271.MirrorCS", {"start": v(-17.43, 109.67) * mm, "mid": v(-11.75, 107.47) * mm, "end": v(-7.05, 103.6) * mm});
            skArc(sketch, "E272.MirrorCS", {"start": v(-82.57, 72.39) * mm, "mid": v(-88.25, 74.59) * mm, "end": v(-92.95, 78.47) * mm});
            skArc(sketch, "E273.MirrorCS", {"start": v(-82.57, 72.39) * mm, "mid": v(-88.28, 61.9) * mm, "end": v(-90.7, 50.22) * mm});
            skLineSegment(sketch, "E274.MirrorCS", {"start": v(-92.95, 78.47) * mm, "end": v(-92.95, 50.22) * mm});
            skLineSegment(sketch, "E275.MirrorCS", {"start": v(-92.95, 17.25) * mm, "end": v(-92.95, 45.5) * mm});
            skArc(sketch, "E276.MirrorCS", {"start": v(-82.57, 23.33) * mm, "mid": v(-88.28, 33.81) * mm, "end": v(-90.7, 45.5) * mm});
            skArc(sketch, "E277.MirrorCS", {"start": v(-82.57, 23.33) * mm, "mid": v(-88.25, 21.13) * mm, "end": v(-92.95, 17.25) * mm});
            skArc(sketch, "E278.MirrorCS", {"start": v(-17.43, 23.33) * mm, "mid": v(-11.72, 33.81) * mm, "end": v(-9.3, 45.5) * mm});
            skArc(sketch, "E279.MirrorCS", {"start": v(-17.43, 23.33) * mm, "mid": v(-11.75, 21.13) * mm, "end": v(-7.05, 17.25) * mm});
            skLineSegment(sketch, "E280.MirrorCS", {"start": v(-7.05, 17.25) * mm, "end": v(-7.05, 45.5) * mm});
            skLineSegment(sketch, "E281.MirrorCS", {"start": v(-7.05, 78.47) * mm, "end": v(-7.05, 50.22) * mm});
            skArc(sketch, "E282.MirrorCS", {"start": v(-17.43, 72.39) * mm, "mid": v(-11.72, 61.9) * mm, "end": v(-9.3, 50.22) * mm});
            skLineSegment(sketch, "E283.MirrorCS", {"start": v(-9.3, 45.5) * mm, "end": v(-7.05, 45.5) * mm});
            skLineSegment(sketch, "E284.MirrorCS", {"start": v(-9.3, 50.22) * mm, "end": v(-7.05, 50.22) * mm});
            skLineSegment(sketch, "E285.MirrorCS", {"start": v(-90.7, 45.5) * mm, "end": v(-92.95, 45.5) * mm});
            skLineSegment(sketch, "E286.MirrorCS", {"start": v(-90.7, 50.22) * mm, "end": v(-92.95, 50.22) * mm});
            skArc(sketch, "E287.MirrorCS", {"start": v(-17.43, 72.39) * mm, "mid": v(-11.75, 74.59) * mm, "end": v(-7.05, 78.47) * mm});
            skArc(sketch, "E288", {"start": v(-22.2, 107.7) * mm, "mid": v(-16.77, 95.87) * mm, "end": v(-4.69, 91.03) * mm});
            skSolve(sketch);
        }
        {
            var Q0;
            Q0=makeQuery(id+"F0.imprint","IMPRINT",FACE,{"disambiguationData":[TD([[makeQuery(id+"F0.imprint","IMPRINT",EDGE,{"derivedFrom":sQuery(id+"F0.wireOp",EDGE,"E15.0")}),-1.0]])]});
            var Q1;
            {var subQ11=sQuery(id+"F0.wireOp",EDGE,"E21");var subQ14=sQuery(id+"F0.wireOp",EDGE,"E20");var subQ17=makeQuery(id+"F0.imprint","INTERSECT",VERTEX,{"derivedFrom":[subQ14,subQ11]});Q1=makeQuery(id+"F0.imprint","IMPRINT",FACE,{"disambiguationData":[TD([[makeQuery(id+"F0.imprint","IMPRINT",EDGE,{"disambiguationData":[TD([[subQ17,1.0]])],"derivedFrom":subQ14}),-1.0]])]});}
            var Q2;
            Q2=makeQuery(id+"F0.imprint","IMPRINT",FACE,{"disambiguationData":[TD([[makeQuery(id+"F0.imprint","IMPRINT",EDGE,{"derivedFrom":sQuery(id+"F0.wireOp",EDGE,"E88.MirrorCS")}),1.0]])]});
            var Q3;
            Q3=makeQuery(id+"F0.imprint","IMPRINT",FACE,{"disambiguationData":[TD([[makeQuery(id+"F0.imprint","IMPRINT",EDGE,{"derivedFrom":sQuery(id+"F0.wireOp",EDGE,"E105.MirrorCS")}),-1.0]])]});
            extrude(context, id + "F1", {"entities" : qUnion([Q0, Q1, Q2, Q3]), "depth" : 1.27 * mm});
        }
        {
            var Q0;
            Q0=makeQuery(id+"F1.opExtrude","CAP_FACE",FACE,{"disambiguationData":[OSD([sQuery(id+"F0.wireOp",EDGE,"evjlkytM-gipT-BmRl-lq5l-QpbO8cgYkB3r"),sQuery(id+"F0.wireOp",EDGE,"E15.0")])],"isStart":false});
            var Q1;
            Q1=makeQuery(id+"F1.opExtrude","CAP_FACE",FACE,{"disambiguationData":[OSD([sQuery(id+"F0.wireOp",EDGE,"E105.MirrorCS"),sQuery(id+"F0.wireOp",EDGE,"E108.MirrorCS"),sQuery(id+"F0.wireOp",EDGE,"E109.MirrorCS"),sQuery(id+"F0.wireOp",EDGE,"E112.MirrorCS"),sQuery(id+"F0.wireOp",EDGE,"E113.MirrorCS"),sQuery(id+"F0.wireOp",EDGE,"E114.MirrorCS"),sQuery(id+"F0.wireOp",EDGE,"E122.MirrorC"),sQuery(id+"F0.wireOp",EDGE,"E151.MirrorCS"),sQuery(id+"F0.wireOp",EDGE,"E191.MirrorCS")])],"isStart":false});
            fillet(context, id + "F2", {"entities" : qUnion([Q0, Q1]), "radius" : 0.5 * mm, "tangentPropagation" : true, "allowEdgeOverflow" : false});
        }
        {
            var Q0;
            {var subQ3=sQuery(id+"F0.wireOp",EDGE,"E30");Q0=makeQuery(id+"F0.imprint","IMPRINT",FACE,{"disambiguationData":[TD([[makeQuery(id+"F0.imprint","IMPRINT",EDGE,{"derivedFrom":subQ3}),1.0]])]});}
            var Q1;
            {var subQ4=sQuery(id+"F0.wireOp",EDGE,"E28");Q1=makeQuery(id+"F0.imprint","IMPRINT",FACE,{"disambiguationData":[TD([[makeQuery(id+"F0.imprint","IMPRINT",EDGE,{"derivedFrom":subQ4}),-1.0]])]});}
            var Q2;
            {var subQ4=sQuery(id+"F0.wireOp",EDGE,"E34");Q2=makeQuery(id+"F0.imprint","IMPRINT",FACE,{"disambiguationData":[TD([[makeQuery(id+"F0.imprint","IMPRINT",EDGE,{"derivedFrom":subQ4}),-1.0]])]});}
            var Q3;
            {var subQ4=sQuery(id+"F0.wireOp",EDGE,"E32");Q3=makeQuery(id+"F0.imprint","IMPRINT",FACE,{"disambiguationData":[TD([[makeQuery(id+"F0.imprint","IMPRINT",EDGE,{"derivedFrom":subQ4}),-1.0]])]});}
            var Q4;
            {var subQ4=sQuery(id+"F0.wireOp",EDGE,"E116.MirrorCS");Q4=makeQuery(id+"F0.imprint","IMPRINT",FACE,{"disambiguationData":[TD([[makeQuery(id+"F0.imprint","IMPRINT",EDGE,{"derivedFrom":subQ4}),-1.0]])]});}
            var Q5;
            {var subQ0=sQuery(id+"F0.wireOp",EDGE,"E106.MirrorCS");Q5=makeQuery(id+"F0.imprint","IMPRINT",FACE,{"disambiguationData":[TD([[makeQuery(id+"F0.imprint","IMPRINT",EDGE,{"derivedFrom":subQ0}),-1.0]])]});}
            var Q6;
            {var subQ3=sQuery(id+"F0.wireOp",EDGE,"E103.MirrorCS");Q6=makeQuery(id+"F0.imprint","IMPRINT",FACE,{"disambiguationData":[TD([[makeQuery(id+"F0.imprint","IMPRINT",EDGE,{"derivedFrom":subQ3}),1.0]])]});}
            var Q7;
            {var subQ3=sQuery(id+"F0.wireOp",EDGE,"E102.MirrorCS");Q7=makeQuery(id+"F0.imprint","IMPRINT",FACE,{"disambiguationData":[TD([[makeQuery(id+"F0.imprint","IMPRINT",EDGE,{"derivedFrom":subQ3}),-1.0]])]});}
            extrude(context, id + "F3", {"entities" : qUnion([Q0, Q1, Q2, Q3, Q4, Q5, Q6, Q7]), "depth" : 1.27 * mm});
        }
        {
            var Q0;
            {var subQ3=sQuery(id+"F0.wireOp",EDGE,"E32");Q0=makeQuery(id+"F0.imprint","IMPRINT",FACE,{"disambiguationData":[TD([[makeQuery(id+"F0.imprint","IMPRINT",EDGE,{"derivedFrom":subQ3}),1.0]])]});}
            var Q1;
            {var subQ3=sQuery(id+"F0.wireOp",EDGE,"E30");Q1=makeQuery(id+"F0.imprint","IMPRINT",FACE,{"disambiguationData":[TD([[makeQuery(id+"F0.imprint","IMPRINT",EDGE,{"derivedFrom":subQ3}),-1.0]])]});}
            var Q2;
            {var subQ3=sQuery(id+"F0.wireOp",EDGE,"E31");Q2=makeQuery(id+"F0.imprint","IMPRINT",FACE,{"disambiguationData":[TD([[makeQuery(id+"F0.imprint","IMPRINT",EDGE,{"derivedFrom":subQ3}),1.0]])]});}
            var Q3;
            {var subQ3=sQuery(id+"F0.wireOp",EDGE,"E29");Q3=makeQuery(id+"F0.imprint","IMPRINT",FACE,{"disambiguationData":[TD([[makeQuery(id+"F0.imprint","IMPRINT",EDGE,{"derivedFrom":subQ3}),-1.0]])]});}
            var Q4;
            {var subQ3=sQuery(id+"F0.wireOp",EDGE,"E28");Q4=makeQuery(id+"F0.imprint","IMPRINT",FACE,{"disambiguationData":[TD([[makeQuery(id+"F0.imprint","IMPRINT",EDGE,{"derivedFrom":subQ3}),1.0]])]});}
            var Q5;
            {var subQ3=sQuery(id+"F0.wireOp",EDGE,"E35");Q5=makeQuery(id+"F0.imprint","IMPRINT",FACE,{"disambiguationData":[TD([[makeQuery(id+"F0.imprint","IMPRINT",EDGE,{"derivedFrom":subQ3}),-1.0]])]});}
            var Q6;
            {var subQ3=sQuery(id+"F0.wireOp",EDGE,"E34");Q6=makeQuery(id+"F0.imprint","IMPRINT",FACE,{"disambiguationData":[TD([[makeQuery(id+"F0.imprint","IMPRINT",EDGE,{"derivedFrom":subQ3}),1.0]])]});}
            var Q7;
            {var subQ3=sQuery(id+"F0.wireOp",EDGE,"E33");Q7=makeQuery(id+"F0.imprint","IMPRINT",FACE,{"disambiguationData":[TD([[makeQuery(id+"F0.imprint","IMPRINT",EDGE,{"derivedFrom":subQ3}),-1.0]])]});}
            var Q8;
            {var subQ0=sQuery(id+"F0.wireOp",EDGE,"E116.MirrorCS");Q8=makeQuery(id+"F0.imprint","IMPRINT",FACE,{"disambiguationData":[TD([[makeQuery(id+"F0.imprint","IMPRINT",EDGE,{"derivedFrom":subQ0}),1.0]])]});}
            var Q9;
            {var subQ0=sQuery(id+"F0.wireOp",EDGE,"E107.MirrorCS");Q9=makeQuery(id+"F0.imprint","IMPRINT",FACE,{"disambiguationData":[TD([[makeQuery(id+"F0.imprint","IMPRINT",EDGE,{"derivedFrom":subQ0}),-1.0]])]});}
            var Q10;
            {var subQ0=sQuery(id+"F0.wireOp",EDGE,"E106.MirrorCS");Q10=makeQuery(id+"F0.imprint","IMPRINT",FACE,{"disambiguationData":[TD([[makeQuery(id+"F0.imprint","IMPRINT",EDGE,{"derivedFrom":subQ0}),1.0]])]});}
            var Q11;
            {var subQ3=sQuery(id+"F0.wireOp",EDGE,"E103.MirrorCS");Q11=makeQuery(id+"F0.imprint","IMPRINT",FACE,{"disambiguationData":[TD([[makeQuery(id+"F0.imprint","IMPRINT",EDGE,{"derivedFrom":subQ3}),-1.0]])]});}
            var Q12;
            {var subQ3=sQuery(id+"F0.wireOp",EDGE,"E117.MirrorCS");Q12=makeQuery(id+"F0.imprint","IMPRINT",FACE,{"disambiguationData":[TD([[makeQuery(id+"F0.imprint","IMPRINT",EDGE,{"derivedFrom":subQ3}),1.0]])]});}
            var Q13;
            {var subQ3=sQuery(id+"F0.wireOp",EDGE,"E115.MirrorCS");Q13=makeQuery(id+"F0.imprint","IMPRINT",FACE,{"disambiguationData":[TD([[makeQuery(id+"F0.imprint","IMPRINT",EDGE,{"derivedFrom":subQ3}),-1.0]])]});}
            var Q14;
            {var subQ3=sQuery(id+"F0.wireOp",EDGE,"E102.MirrorCS");Q14=makeQuery(id+"F0.imprint","IMPRINT",FACE,{"disambiguationData":[TD([[makeQuery(id+"F0.imprint","IMPRINT",EDGE,{"derivedFrom":subQ3}),1.0]])]});}
            var Q15;
            {var subQ3=sQuery(id+"F0.wireOp",EDGE,"E119.MirrorCS");Q15=makeQuery(id+"F0.imprint","IMPRINT",FACE,{"disambiguationData":[TD([[makeQuery(id+"F0.imprint","IMPRINT",EDGE,{"derivedFrom":subQ3}),-1.0]])]});}
            extrude(context, id + "F4", {"entities" : qUnion([Q0, Q1, Q2, Q3, Q4, Q5, Q6, Q7, Q8, Q9, Q10, Q11, Q12, Q13, Q14, Q15]), "depth" : 1.27 * mm});
        }
        {
            var Q0;
            Q0=makeQuery(id+"F0.imprint","IMPRINT",FACE,{"disambiguationData":[TD([[makeQuery(id+"F0.imprint","IMPRINT",EDGE,{"derivedFrom":sQuery(id+"F0.wireOp",EDGE,"E36.0")}),-1.0]])]});
            var Q1;
            Q1=makeQuery(id+"F0.imprint","IMPRINT",FACE,{"disambiguationData":[TD([[makeQuery(id+"F0.imprint","IMPRINT",EDGE,{"derivedFrom":sQuery(id+"F0.wireOp",EDGE,"E88.MirrorCS")}),-1.0]])]});
            extrude(context, id + "F5", {"entities" : qUnion([Q0, Q1]), "depth" : 1.27 * mm});
        }
        {
            var Q0;
            Q0=makeQuery(id+"F5.opExtrude","CAP_FACE",FACE,{"disambiguationData":[OSD([sQuery(id+"F0.wireOp",EDGE,"E36.0"),sQuery(id+"F0.wireOp",EDGE,"E36.1"),sQuery(id+"F0.wireOp",EDGE,"E36.2"),sQuery(id+"F0.wireOp",EDGE,"E36.3"),sQuery(id+"F0.wireOp",EDGE,"E36.4"),sQuery(id+"F0.wireOp",EDGE,"E36.5"),sQuery(id+"F0.wireOp",EDGE,"E36.6"),sQuery(id+"F0.wireOp",EDGE,"E36.7")])],"isStart":false});
            var Q1;
            Q1=makeQuery(id+"F5.opExtrude","CAP_FACE",FACE,{"disambiguationData":[OSD([sQuery(id+"F0.wireOp",EDGE,"E88.MirrorCS"),sQuery(id+"F0.wireOp",EDGE,"E89.MirrorCS"),sQuery(id+"F0.wireOp",EDGE,"E90.MirrorCS"),sQuery(id+"F0.wireOp",EDGE,"E91.MirrorCS"),sQuery(id+"F0.wireOp",EDGE,"E92.MirrorCS"),sQuery(id+"F0.wireOp",EDGE,"E93.MirrorCS"),sQuery(id+"F0.wireOp",EDGE,"E94.MirrorCS"),sQuery(id+"F0.wireOp",EDGE,"E95.MirrorCS")])],"isStart":false});
            extrude(context, id + "F6", {"entities" : qUnion([Q0, Q1]), "depth" : 0.25 * mm});
        }
        {
            var Q0;
            Q0=makeQuery(id+"F6.opExtrude","CAP_FACE",FACE,{"disambiguationData":[OSD([sQuery(id+"F0.wireOp",EDGE,"E36.0"),sQuery(id+"F0.wireOp",EDGE,"E36.1"),sQuery(id+"F0.wireOp",EDGE,"E36.2"),sQuery(id+"F0.wireOp",EDGE,"E36.3"),sQuery(id+"F0.wireOp",EDGE,"E36.4"),sQuery(id+"F0.wireOp",EDGE,"E36.5"),sQuery(id+"F0.wireOp",EDGE,"E36.6"),sQuery(id+"F0.wireOp",EDGE,"E36.7")])],"isStart":false});
            var Q1;
            Q1=makeQuery(id+"F6.opExtrude","CAP_FACE",FACE,{"disambiguationData":[OSD([sQuery(id+"F0.wireOp",EDGE,"E88.MirrorCS"),sQuery(id+"F0.wireOp",EDGE,"E89.MirrorCS"),sQuery(id+"F0.wireOp",EDGE,"E90.MirrorCS"),sQuery(id+"F0.wireOp",EDGE,"E91.MirrorCS"),sQuery(id+"F0.wireOp",EDGE,"E92.MirrorCS"),sQuery(id+"F0.wireOp",EDGE,"E93.MirrorCS"),sQuery(id+"F0.wireOp",EDGE,"E94.MirrorCS"),sQuery(id+"F0.wireOp",EDGE,"E95.MirrorCS")])],"isStart":false});
            fillet(context, id + "F7", {"entities" : qUnion([Q0, Q1]), "radius" : 0.25 * mm, "tangentPropagation" : true, "defaultsChanged" : false, "vertexSettings" : [], "allowEdgeOverflow" : false});
        }
        {
            var Q0;
            Q0=makeQuery(id+"F1.opExtrude","CAP_EDGE",EDGE,{"disambiguationData":[OSD([sQuery(id+"F0.wireOp",EDGE,"E21")])],"isStart":false});
            var Q1;
            Q1=makeQuery(id+"F1.opExtrude","CAP_EDGE",EDGE,{"disambiguationData":[OSD([sQuery(id+"F0.wireOp",EDGE,"E22")])],"isStart":false});
            var Q2;
            Q2=makeQuery(id+"F1.opExtrude","CAP_EDGE",EDGE,{"disambiguationData":[OSD([sQuery(id+"F0.wireOp",EDGE,"E23")])],"isStart":false});
            var Q3;
            Q3=makeQuery(id+"F1.opExtrude","CAP_EDGE",EDGE,{"disambiguationData":[OSD([sQuery(id+"F0.wireOp",EDGE,"E24")])],"isStart":false});
            var Q4;
            Q4=makeQuery(id+"F1.opExtrude","CAP_EDGE",EDGE,{"disambiguationData":[OSD([sQuery(id+"F0.wireOp",EDGE,"E25")])],"isStart":false});
            var Q5;
            Q5=makeQuery(id+"F1.opExtrude","CAP_EDGE",EDGE,{"disambiguationData":[OSD([sQuery(id+"F0.wireOp",EDGE,"E26")])],"isStart":false});
            var Q6;
            Q6=makeQuery(id+"F1.opExtrude","CAP_EDGE",EDGE,{"disambiguationData":[OSD([sQuery(id+"F0.wireOp",EDGE,"E27")])],"isStart":false});
            var Q7;
            Q7=makeQuery(id+"F1.opExtrude","CAP_EDGE",EDGE,{"disambiguationData":[OSD([sQuery(id+"F0.wireOp",EDGE,"E20")])],"isStart":false});
            var Q8;
            Q8=makeQuery(id+"F1.opExtrude","CAP_EDGE",EDGE,{"disambiguationData":[OSD([sQuery(id+"F0.wireOp",EDGE,"E104.MirrorCS")])],"isStart":false});
            var Q9;
            Q9=makeQuery(id+"F1.opExtrude","CAP_EDGE",EDGE,{"disambiguationData":[OSD([sQuery(id+"F0.wireOp",EDGE,"E101.MirrorCS")])],"isStart":false});
            var Q10;
            Q10=makeQuery(id+"F1.opExtrude","CAP_EDGE",EDGE,{"disambiguationData":[OSD([sQuery(id+"F0.wireOp",EDGE,"E110.MirrorCS")])],"isStart":false});
            var Q11;
            Q11=makeQuery(id+"F1.opExtrude","CAP_EDGE",EDGE,{"disambiguationData":[OSD([sQuery(id+"F0.wireOp",EDGE,"E111.MirrorCS")])],"isStart":false});
            var Q12;
            Q12=makeQuery(id+"F1.opExtrude","CAP_EDGE",EDGE,{"disambiguationData":[OSD([sQuery(id+"F0.wireOp",EDGE,"E99.MirrorCS")])],"isStart":false});
            var Q13;
            Q13=makeQuery(id+"F1.opExtrude","CAP_EDGE",EDGE,{"disambiguationData":[OSD([sQuery(id+"F0.wireOp",EDGE,"E118.MirrorCS")])],"isStart":false});
            var Q14;
            Q14=makeQuery(id+"F1.opExtrude","CAP_EDGE",EDGE,{"disambiguationData":[OSD([sQuery(id+"F0.wireOp",EDGE,"E96.MirrorCS")])],"isStart":false});
            var Q15;
            Q15=makeQuery(id+"F1.opExtrude","CAP_EDGE",EDGE,{"disambiguationData":[OSD([sQuery(id+"F0.wireOp",EDGE,"E100.MirrorCS")])],"isStart":false});
            fillet(context, id + "F8", {"entities" : qUnion([Q0, Q1, Q2, Q3, Q4, Q5, Q6, Q7, Q8, Q9, Q10, Q11, Q12, Q13, Q14, Q15]), "radius" : 0.5 * mm, "tangentPropagation" : true, "allowEdgeOverflow" : false});
        }
        {
            var Q0;
            Q0=makeQuery(id+"F3.opExtrude","CAP_FACE",FACE,{"disambiguationData":[OSD([sQuery(id+"F0.wireOp",EDGE,"E20"),sQuery(id+"F0.wireOp",EDGE,"E21"),sQuery(id+"F0.wireOp",EDGE,"E30"),sQuery(id+"F0.wireOp",EDGE,"E31")])],"isStart":false});
            var Q1;
            Q1=makeQuery(id+"F3.opExtrude","CAP_FACE",FACE,{"disambiguationData":[OSD([sQuery(id+"F0.wireOp",EDGE,"E26"),sQuery(id+"F0.wireOp",EDGE,"E27"),sQuery(id+"F0.wireOp",EDGE,"E32"),sQuery(id+"F0.wireOp",EDGE,"E33")])],"isStart":false});
            var Q2;
            Q2=makeQuery(id+"F3.opExtrude","CAP_FACE",FACE,{"disambiguationData":[OSD([sQuery(id+"F0.wireOp",EDGE,"E24"),sQuery(id+"F0.wireOp",EDGE,"E25"),sQuery(id+"F0.wireOp",EDGE,"E34"),sQuery(id+"F0.wireOp",EDGE,"E35")])],"isStart":false});
            var Q3;
            Q3=makeQuery(id+"F3.opExtrude","CAP_FACE",FACE,{"disambiguationData":[OSD([sQuery(id+"F0.wireOp",EDGE,"E22"),sQuery(id+"F0.wireOp",EDGE,"E23"),sQuery(id+"F0.wireOp",EDGE,"E28"),sQuery(id+"F0.wireOp",EDGE,"E29")])],"isStart":false});
            var Q4;
            Q4=makeQuery(id+"F3.opExtrude","CAP_FACE",FACE,{"disambiguationData":[OSD([sQuery(id+"F0.wireOp",EDGE,"E106.MirrorCS"),sQuery(id+"F0.wireOp",EDGE,"E107.MirrorCS"),sQuery(id+"F0.wireOp",EDGE,"E110.MirrorCS"),sQuery(id+"F0.wireOp",EDGE,"E111.MirrorCS")])],"isStart":false});
            var Q5;
            Q5=makeQuery(id+"F3.opExtrude","CAP_FACE",FACE,{"disambiguationData":[OSD([sQuery(id+"F0.wireOp",EDGE,"E99.MirrorCS"),sQuery(id+"F0.wireOp",EDGE,"E116.MirrorCS"),sQuery(id+"F0.wireOp",EDGE,"E118.MirrorCS"),sQuery(id+"F0.wireOp",EDGE,"E119.MirrorCS")])],"isStart":false});
            var Q6;
            Q6=makeQuery(id+"F3.opExtrude","CAP_FACE",FACE,{"disambiguationData":[OSD([sQuery(id+"F0.wireOp",EDGE,"E96.MirrorCS"),sQuery(id+"F0.wireOp",EDGE,"E100.MirrorCS"),sQuery(id+"F0.wireOp",EDGE,"E102.MirrorCS"),sQuery(id+"F0.wireOp",EDGE,"E115.MirrorCS")])],"isStart":false});
            var Q7;
            Q7=makeQuery(id+"F3.opExtrude","CAP_FACE",FACE,{"disambiguationData":[OSD([sQuery(id+"F0.wireOp",EDGE,"E101.MirrorCS"),sQuery(id+"F0.wireOp",EDGE,"E103.MirrorCS"),sQuery(id+"F0.wireOp",EDGE,"E104.MirrorCS"),sQuery(id+"F0.wireOp",EDGE,"E117.MirrorCS")])],"isStart":false});
            fillet(context, id + "F9", {"entities" : qUnion([Q0, Q1, Q2, Q3, Q4, Q5, Q6, Q7]), "radius" : 0.25 * mm, "tangentPropagation" : true, "allowEdgeOverflow" : false});
        }
        {
            var Q0;
            Q0=makeQuery(id+"F4.opExtrude","CAP_FACE",FACE,{"disambiguationData":[OSD([sQuery(id+"F0.wireOp",EDGE,"E15.0"),sQuery(id+"F0.wireOp",EDGE,"E26"),sQuery(id+"F0.wireOp",EDGE,"E33")])],"isStart":false});
            var Q1;
            Q1=makeQuery(id+"F4.opExtrude","CAP_FACE",FACE,{"disambiguationData":[OSD([sQuery(id+"F0.wireOp",EDGE,"E15.0"),sQuery(id+"F0.wireOp",EDGE,"E25"),sQuery(id+"F0.wireOp",EDGE,"E34")])],"isStart":false});
            var Q2;
            Q2=makeQuery(id+"F4.opExtrude","CAP_FACE",FACE,{"disambiguationData":[OSD([sQuery(id+"F0.wireOp",EDGE,"E15.0"),sQuery(id+"F0.wireOp",EDGE,"E24"),sQuery(id+"F0.wireOp",EDGE,"E35")])],"isStart":false});
            var Q3;
            Q3=makeQuery(id+"F4.opExtrude","CAP_FACE",FACE,{"disambiguationData":[OSD([sQuery(id+"F0.wireOp",EDGE,"E15.0"),sQuery(id+"F0.wireOp",EDGE,"E23"),sQuery(id+"F0.wireOp",EDGE,"E28")])],"isStart":false});
            var Q4;
            Q4=makeQuery(id+"F4.opExtrude","CAP_FACE",FACE,{"disambiguationData":[OSD([sQuery(id+"F0.wireOp",EDGE,"E15.0"),sQuery(id+"F0.wireOp",EDGE,"E22"),sQuery(id+"F0.wireOp",EDGE,"E29")])],"isStart":false});
            var Q5;
            Q5=makeQuery(id+"F4.opExtrude","CAP_FACE",FACE,{"disambiguationData":[OSD([sQuery(id+"F0.wireOp",EDGE,"E15.0"),sQuery(id+"F0.wireOp",EDGE,"E21"),sQuery(id+"F0.wireOp",EDGE,"E31")])],"isStart":false});
            var Q6;
            Q6=makeQuery(id+"F4.opExtrude","CAP_FACE",FACE,{"disambiguationData":[OSD([sQuery(id+"F0.wireOp",EDGE,"E15.0"),sQuery(id+"F0.wireOp",EDGE,"E20"),sQuery(id+"F0.wireOp",EDGE,"E30")])],"isStart":false});
            var Q7;
            Q7=makeQuery(id+"F4.opExtrude","CAP_FACE",FACE,{"disambiguationData":[OSD([sQuery(id+"F0.wireOp",EDGE,"E15.0"),sQuery(id+"F0.wireOp",EDGE,"E27"),sQuery(id+"F0.wireOp",EDGE,"E32")])],"isStart":false});
            var Q8;
            Q8=makeQuery(id+"F4.opExtrude","CAP_FACE",FACE,{"disambiguationData":[OSD([sQuery(id+"F0.wireOp",EDGE,"E104.MirrorCS"),sQuery(id+"F0.wireOp",EDGE,"E117.MirrorCS"),sQuery(id+"F0.wireOp",EDGE,"E122.MirrorC")])],"isStart":false});
            var Q9;
            Q9=makeQuery(id+"F4.opExtrude","CAP_FACE",FACE,{"disambiguationData":[OSD([sQuery(id+"F0.wireOp",EDGE,"E101.MirrorCS"),sQuery(id+"F0.wireOp",EDGE,"E103.MirrorCS"),sQuery(id+"F0.wireOp",EDGE,"E122.MirrorC")])],"isStart":false});
            var Q10;
            Q10=makeQuery(id+"F4.opExtrude","CAP_FACE",FACE,{"disambiguationData":[OSD([sQuery(id+"F0.wireOp",EDGE,"E106.MirrorCS"),sQuery(id+"F0.wireOp",EDGE,"E110.MirrorCS"),sQuery(id+"F0.wireOp",EDGE,"E122.MirrorC")])],"isStart":false});
            var Q11;
            Q11=makeQuery(id+"F4.opExtrude","CAP_FACE",FACE,{"disambiguationData":[OSD([sQuery(id+"F0.wireOp",EDGE,"E107.MirrorCS"),sQuery(id+"F0.wireOp",EDGE,"E111.MirrorCS"),sQuery(id+"F0.wireOp",EDGE,"E122.MirrorC")])],"isStart":false});
            var Q12;
            Q12=makeQuery(id+"F4.opExtrude","CAP_FACE",FACE,{"disambiguationData":[OSD([sQuery(id+"F0.wireOp",EDGE,"E116.MirrorCS"),sQuery(id+"F0.wireOp",EDGE,"E118.MirrorCS"),sQuery(id+"F0.wireOp",EDGE,"E122.MirrorC")])],"isStart":false});
            var Q13;
            Q13=makeQuery(id+"F4.opExtrude","CAP_FACE",FACE,{"disambiguationData":[OSD([sQuery(id+"F0.wireOp",EDGE,"E99.MirrorCS"),sQuery(id+"F0.wireOp",EDGE,"E119.MirrorCS"),sQuery(id+"F0.wireOp",EDGE,"E122.MirrorC")])],"isStart":false});
            var Q14;
            Q14=makeQuery(id+"F4.opExtrude","CAP_FACE",FACE,{"disambiguationData":[OSD([sQuery(id+"F0.wireOp",EDGE,"E96.MirrorCS"),sQuery(id+"F0.wireOp",EDGE,"E102.MirrorCS"),sQuery(id+"F0.wireOp",EDGE,"E122.MirrorC")])],"isStart":false});
            var Q15;
            Q15=makeQuery(id+"F4.opExtrude","CAP_FACE",FACE,{"disambiguationData":[OSD([sQuery(id+"F0.wireOp",EDGE,"E100.MirrorCS"),sQuery(id+"F0.wireOp",EDGE,"E115.MirrorCS"),sQuery(id+"F0.wireOp",EDGE,"E122.MirrorC")])],"isStart":false});
            fillet(context, id + "F10", {"entities" : qUnion([Q0, Q1, Q2, Q3, Q4, Q5, Q6, Q7, Q8, Q9, Q10, Q11, Q12, Q13, Q14, Q15]), "radius" : 0.25 * mm, "tangentPropagation" : true, "allowEdgeOverflow" : false});
        }
        {
            var Q0;
            {var subQ0=sQuery(id+"F0.wireOp",EDGE,"E10");Q0=makeQuery(id+"F0.imprint","IMPRINT",FACE,{"disambiguationData":[TD([[makeQuery(id+"F0.imprint","IMPRINT",EDGE,{"derivedFrom":subQ0}),1.0]])]});}
            var Q1;
            {var subQ0=sQuery(id+"F0.wireOp",EDGE,"E11");Q1=makeQuery(id+"F0.imprint","IMPRINT",FACE,{"disambiguationData":[TD([[makeQuery(id+"F0.imprint","IMPRINT",EDGE,{"derivedFrom":subQ0}),1.0]])]});}
            var Q2;
            {var subQ0=sQuery(id+"F0.wireOp",EDGE,"E8");Q2=makeQuery(id+"F0.imprint","IMPRINT",FACE,{"disambiguationData":[TD([[makeQuery(id+"F0.imprint","IMPRINT",EDGE,{"derivedFrom":subQ0}),-1.0]])]});}
            var Q3;
            {var subQ0=sQuery(id+"F0.wireOp",EDGE,"E7");Q3=makeQuery(id+"F0.imprint","IMPRINT",FACE,{"disambiguationData":[TD([[makeQuery(id+"F0.imprint","IMPRINT",EDGE,{"derivedFrom":subQ0}),-1.0]])]});}
            var Q4;
            Q4=makeQuery(id+"F0.imprint","IMPRINT",FACE,{"disambiguationData":[TD([[makeQuery(id+"F0.imprint","IMPRINT",EDGE,{"derivedFrom":sQuery(id+"F0.wireOp",EDGE,"E108.MirrorCS")}),1.0]])]});
            var Q5;
            Q5=makeQuery(id+"F0.imprint","IMPRINT",FACE,{"disambiguationData":[TD([[makeQuery(id+"F0.imprint","IMPRINT",EDGE,{"derivedFrom":sQuery(id+"F0.wireOp",EDGE,"E105.MirrorCS")}),1.0]])]});
            var Q6;
            Q6=makeQuery(id+"F0.imprint","IMPRINT",FACE,{"disambiguationData":[TD([[makeQuery(id+"F0.imprint","IMPRINT",EDGE,{"derivedFrom":sQuery(id+"F0.wireOp",EDGE,"E124.MirrorCS")}),-1.0]])]});
            var Q7;
            Q7=makeQuery(id+"F0.imprint","IMPRINT",FACE,{"disambiguationData":[TD([[makeQuery(id+"F0.imprint","IMPRINT",EDGE,{"derivedFrom":sQuery(id+"F0.wireOp",EDGE,"E109.MirrorCS")}),1.0]])]});
            extrude(context, id + "F11", {"entities" : qUnion([Q0, Q1, Q2, Q3, Q4, Q5, Q6, Q7]), "depth" : 1.27 * mm});
        }
        {
            var Q0;
            {var subQ0=sQuery(id+"F0.wireOp",EDGE,"E8");Q0=makeQuery(id+"F0.imprint","IMPRINT",FACE,{"disambiguationData":[TD([[makeQuery(id+"F0.imprint","IMPRINT",EDGE,{"derivedFrom":subQ0}),1.0]])]});}
            var Q1;
            {var subQ0=sQuery(id+"F0.wireOp",EDGE,"E9");Q1=makeQuery(id+"F0.imprint","IMPRINT",FACE,{"disambiguationData":[TD([[makeQuery(id+"F0.imprint","IMPRINT",EDGE,{"derivedFrom":subQ0}),-1.0]])]});}
            var Q2;
            {var subQ0=sQuery(id+"F0.wireOp",EDGE,"E11");Q2=makeQuery(id+"F0.imprint","IMPRINT",FACE,{"disambiguationData":[TD([[makeQuery(id+"F0.imprint","IMPRINT",EDGE,{"derivedFrom":subQ0}),-1.0]])]});}
            var Q3;
            {var subQ0=sQuery(id+"F0.wireOp",EDGE,"E7");Q3=makeQuery(id+"F0.imprint","IMPRINT",FACE,{"disambiguationData":[TD([[makeQuery(id+"F0.imprint","IMPRINT",EDGE,{"derivedFrom":subQ0}),1.0]])]});}
            var Q4;
            Q4=makeQuery(id+"F0.imprint","IMPRINT",FACE,{"disambiguationData":[TD([[makeQuery(id+"F0.imprint","IMPRINT",EDGE,{"derivedFrom":sQuery(id+"F0.wireOp",EDGE,"E128.MirrorCS")}),-1.0]])]});
            var Q5;
            Q5=makeQuery(id+"F0.imprint","IMPRINT",FACE,{"disambiguationData":[TD([[makeQuery(id+"F0.imprint","IMPRINT",EDGE,{"derivedFrom":sQuery(id+"F0.wireOp",EDGE,"E112.MirrorCS")}),1.0]])]});
            var Q6;
            Q6=makeQuery(id+"F0.imprint","IMPRINT",FACE,{"disambiguationData":[TD([[makeQuery(id+"F0.imprint","IMPRINT",EDGE,{"derivedFrom":sQuery(id+"F0.wireOp",EDGE,"E113.MirrorCS")}),1.0]])]});
            var Q7;
            Q7=makeQuery(id+"F0.imprint","IMPRINT",FACE,{"disambiguationData":[TD([[makeQuery(id+"F0.imprint","IMPRINT",EDGE,{"derivedFrom":sQuery(id+"F0.wireOp",EDGE,"E114.MirrorCS")}),1.0]])]});
            extrude(context, id + "F12", {"entities" : qUnion([Q0, Q1, Q2, Q3, Q4, Q5, Q6, Q7]), "depth" : 1.27 * mm});
        }
        {
            var Q0;
            Q0=makeQuery(id+"F11.opExtrude","CAP_FACE",FACE,{"disambiguationData":[OSD([sQuery(id+"F0.wireOp",EDGE,"evjlkytM-gipT-BmRl-lq5l-QpbO8cgYkB3r"),sQuery(id+"F0.wireOp",EDGE,"703abfd0-a67d-4bc6-9fe7-a1bc65d53958.0"),sQuery(id+"F0.wireOp",EDGE,"E8"),sQuery(id+"F0.wireOp",EDGE,"E9")])],"isStart":false});
            var Q1;
            Q1=makeQuery(id+"F11.opExtrude","CAP_FACE",FACE,{"disambiguationData":[OSD([sQuery(id+"F0.wireOp",EDGE,"evjlkytM-gipT-BmRl-lq5l-QpbO8cgYkB3r"),sQuery(id+"F0.wireOp",EDGE,"703abfd0-a67d-4bc6-9fe7-a1bc65d53958.0"),sQuery(id+"F0.wireOp",EDGE,"E11"),sQuery(id+"F0.wireOp",EDGE,"E13")])],"isStart":false});
            var Q2;
            Q2=makeQuery(id+"F11.opExtrude","CAP_FACE",FACE,{"disambiguationData":[OSD([sQuery(id+"F0.wireOp",EDGE,"evjlkytM-gipT-BmRl-lq5l-QpbO8cgYkB3r"),sQuery(id+"F0.wireOp",EDGE,"703abfd0-a67d-4bc6-9fe7-a1bc65d53958.0"),sQuery(id+"F0.wireOp",EDGE,"E10"),sQuery(id+"F0.wireOp",EDGE,"E14")])],"isStart":false});
            var Q3;
            Q3=makeQuery(id+"F11.opExtrude","CAP_FACE",FACE,{"disambiguationData":[OSD([sQuery(id+"F0.wireOp",EDGE,"evjlkytM-gipT-BmRl-lq5l-QpbO8cgYkB3r"),sQuery(id+"F0.wireOp",EDGE,"703abfd0-a67d-4bc6-9fe7-a1bc65d53958.0"),sQuery(id+"F0.wireOp",EDGE,"E7"),sQuery(id+"F0.wireOp",EDGE,"E12")])],"isStart":false});
            var Q4;
            Q4=makeQuery(id+"F12.opExtrude","CAP_FACE",FACE,{"disambiguationData":[OSD([sQuery(id+"F0.wireOp",EDGE,"evjlkytM-gipT-BmRl-lq5l-QpbO8cgYkB3r"),sQuery(id+"F0.wireOp",EDGE,"703abfd0-a67d-4bc6-9fe7-a1bc65d53958.0"),sQuery(id+"F0.wireOp",EDGE,"E8"),sQuery(id+"F0.wireOp",EDGE,"E12")])],"isStart":false});
            var Q5;
            Q5=makeQuery(id+"F12.opExtrude","CAP_FACE",FACE,{"disambiguationData":[OSD([sQuery(id+"F0.wireOp",EDGE,"evjlkytM-gipT-BmRl-lq5l-QpbO8cgYkB3r"),sQuery(id+"F0.wireOp",EDGE,"703abfd0-a67d-4bc6-9fe7-a1bc65d53958.0"),sQuery(id+"F0.wireOp",EDGE,"E9"),sQuery(id+"F0.wireOp",EDGE,"E13")])],"isStart":false});
            var Q6;
            Q6=makeQuery(id+"F12.opExtrude","CAP_FACE",FACE,{"disambiguationData":[OSD([sQuery(id+"F0.wireOp",EDGE,"evjlkytM-gipT-BmRl-lq5l-QpbO8cgYkB3r"),sQuery(id+"F0.wireOp",EDGE,"703abfd0-a67d-4bc6-9fe7-a1bc65d53958.0"),sQuery(id+"F0.wireOp",EDGE,"E11"),sQuery(id+"F0.wireOp",EDGE,"E14")])],"isStart":false});
            var Q7;
            Q7=makeQuery(id+"F12.opExtrude","CAP_FACE",FACE,{"disambiguationData":[OSD([sQuery(id+"F0.wireOp",EDGE,"evjlkytM-gipT-BmRl-lq5l-QpbO8cgYkB3r"),sQuery(id+"F0.wireOp",EDGE,"703abfd0-a67d-4bc6-9fe7-a1bc65d53958.0"),sQuery(id+"F0.wireOp",EDGE,"E7"),sQuery(id+"F0.wireOp",EDGE,"E10")])],"isStart":false});
            var Q8;
            Q8=makeQuery(id+"F12.opExtrude","CAP_FACE",FACE,{"disambiguationData":[OSD([sQuery(id+"F0.wireOp",EDGE,"E113.MirrorCS"),sQuery(id+"F0.wireOp",EDGE,"E123.MirrorCS"),sQuery(id+"F0.wireOp",EDGE,"E136.MirrorCS"),sQuery(id+"F0.wireOp",EDGE,"E149.MirrorCS"),sQuery(id+"F0.wireOp",EDGE,"E173.MirrorCS"),sQuery(id+"F0.wireOp",EDGE,"E184.MirrorCS"),sQuery(id+"F0.wireOp",EDGE,"E189.MirrorCS"),sQuery(id+"F0.wireOp",EDGE,"E196.MirrorCS")])],"isStart":false});
            var Q9;
            Q9=makeQuery(id+"F11.opExtrude","CAP_FACE",FACE,{"disambiguationData":[OSD([sQuery(id+"F0.wireOp",EDGE,"E124.MirrorCS"),sQuery(id+"F0.wireOp",EDGE,"E139.MirrorCS"),sQuery(id+"F0.wireOp",EDGE,"E151.MirrorCS"),sQuery(id+"F0.wireOp",EDGE,"E157.MirrorCS"),sQuery(id+"F0.wireOp",EDGE,"E167.MirrorCS"),sQuery(id+"F0.wireOp",EDGE,"E171.MirrorCS"),sQuery(id+"F0.wireOp",EDGE,"E173.MirrorCS"),sQuery(id+"F0.wireOp",EDGE,"E193.MirrorCS")])],"isStart":false});
            var Q10;
            Q10=makeQuery(id+"F12.opExtrude","CAP_FACE",FACE,{"disambiguationData":[OSD([sQuery(id+"F0.wireOp",EDGE,"E112.MirrorCS"),sQuery(id+"F0.wireOp",EDGE,"E127.MirrorCS"),sQuery(id+"F0.wireOp",EDGE,"E145.MirrorCS"),sQuery(id+"F0.wireOp",EDGE,"E163.MirrorCS"),sQuery(id+"F0.wireOp",EDGE,"E171.MirrorCS"),sQuery(id+"F0.wireOp",EDGE,"E174.MirrorCS"),sQuery(id+"F0.wireOp",EDGE,"E177.MirrorCS"),sQuery(id+"F0.wireOp",EDGE,"E183.MirrorCS")])],"isStart":false});
            var Q11;
            Q11=makeQuery(id+"F11.opExtrude","CAP_FACE",FACE,{"disambiguationData":[OSD([sQuery(id+"F0.wireOp",EDGE,"E105.MirrorCS"),sQuery(id+"F0.wireOp",EDGE,"E126.MirrorCS"),sQuery(id+"F0.wireOp",EDGE,"E141.MirrorCS"),sQuery(id+"F0.wireOp",EDGE,"E150.MirrorCS"),sQuery(id+"F0.wireOp",EDGE,"E168.MirrorCS"),sQuery(id+"F0.wireOp",EDGE,"E181.MirrorCS"),sQuery(id+"F0.wireOp",EDGE,"E183.MirrorCS"),sQuery(id+"F0.wireOp",EDGE,"E192.MirrorCS")])],"isStart":false});
            var Q12;
            Q12=makeQuery(id+"F12.opExtrude","CAP_FACE",FACE,{"disambiguationData":[OSD([sQuery(id+"F0.wireOp",EDGE,"E128.MirrorCS"),sQuery(id+"F0.wireOp",EDGE,"E143.MirrorCS"),sQuery(id+"F0.wireOp",EDGE,"E148.MirrorCS"),sQuery(id+"F0.wireOp",EDGE,"E166.MirrorCS"),sQuery(id+"F0.wireOp",EDGE,"E172.MirrorCS"),sQuery(id+"F0.wireOp",EDGE,"E181.MirrorCS"),sQuery(id+"F0.wireOp",EDGE,"E188.MirrorCS"),sQuery(id+"F0.wireOp",EDGE,"E191.MirrorCS")])],"isStart":false});
            var Q13;
            Q13=makeQuery(id+"F11.opExtrude","CAP_FACE",FACE,{"disambiguationData":[OSD([sQuery(id+"F0.wireOp",EDGE,"E108.MirrorCS"),sQuery(id+"F0.wireOp",EDGE,"E125.MirrorCS"),sQuery(id+"F0.wireOp",EDGE,"E137.MirrorCS"),sQuery(id+"F0.wireOp",EDGE,"E152.MirrorCS"),sQuery(id+"F0.wireOp",EDGE,"E153.MirrorCS"),sQuery(id+"F0.wireOp",EDGE,"E155.MirrorCS"),sQuery(id+"F0.wireOp",EDGE,"E186.MirrorCS"),sQuery(id+"F0.wireOp",EDGE,"E188.MirrorCS")])],"isStart":false});
            var Q14;
            Q14=makeQuery(id+"F12.opExtrude","CAP_FACE",FACE,{"disambiguationData":[OSD([sQuery(id+"F0.wireOp",EDGE,"E114.MirrorCS"),sQuery(id+"F0.wireOp",EDGE,"E120.MirrorCS"),sQuery(id+"F0.wireOp",EDGE,"E140.MirrorCS"),sQuery(id+"F0.wireOp",EDGE,"E162.MirrorCS"),sQuery(id+"F0.wireOp",EDGE,"E185.MirrorCS"),sQuery(id+"F0.wireOp",EDGE,"E186.MirrorCS"),sQuery(id+"F0.wireOp",EDGE,"E194.MirrorCS"),sQuery(id+"F0.wireOp",EDGE,"E195.MirrorCS")])],"isStart":false});
            var Q15;
            Q15=makeQuery(id+"F11.opExtrude","CAP_FACE",FACE,{"disambiguationData":[OSD([sQuery(id+"F0.wireOp",EDGE,"E109.MirrorCS"),sQuery(id+"F0.wireOp",EDGE,"E121.MirrorCS"),sQuery(id+"F0.wireOp",EDGE,"E147.MirrorCS"),sQuery(id+"F0.wireOp",EDGE,"E156.MirrorCS"),sQuery(id+"F0.wireOp",EDGE,"E158.MirrorCS"),sQuery(id+"F0.wireOp",EDGE,"E180.MirrorCS"),sQuery(id+"F0.wireOp",EDGE,"E194.MirrorCS"),sQuery(id+"F0.wireOp",EDGE,"E196.MirrorCS")])],"isStart":false});
            fillet(context, id + "F13", {"entities" : qUnion([Q0, Q1, Q2, Q3, Q4, Q5, Q6, Q7, Q8, Q9, Q10, Q11, Q12, Q13, Q14, Q15]), "radius" : 0.5 * mm, "tangentPropagation" : true, "allowEdgeOverflow" : false});
        }
        {
            var Q0;
            Q0=makeQuery(id+"F0.imprint","IMPRINT",FACE,{"disambiguationData":[TD([[makeQuery(id+"F0.imprint","IMPRINT",EDGE,{"derivedFrom":sQuery(id+"F0.wireOp",EDGE,"E72.0")}),-1.0]])]});
            var Q1;
            Q1=makeQuery(id+"F0.imprint","IMPRINT",FACE,{"disambiguationData":[TD([[makeQuery(id+"F0.imprint","IMPRINT",EDGE,{"derivedFrom":sQuery(id+"F0.wireOp",EDGE,"E74.0")}),1.0]])]});
            var Q2;
            Q2=makeQuery(id+"F0.imprint","IMPRINT",FACE,{"disambiguationData":[TD([[makeQuery(id+"F0.imprint","IMPRINT",EDGE,{"derivedFrom":sQuery(id+"F0.wireOp",EDGE,"E82.0")}),1.0]])]});
            var Q3;
            Q3=makeQuery(id+"F0.imprint","IMPRINT",FACE,{"disambiguationData":[TD([[makeQuery(id+"F0.imprint","IMPRINT",EDGE,{"derivedFrom":sQuery(id+"F0.wireOp",EDGE,"E84.0")}),1.0]])]});
            var Q4;
            Q4=makeQuery(id+"F0.imprint","IMPRINT",FACE,{"disambiguationData":[TD([[makeQuery(id+"F0.imprint","IMPRINT",EDGE,{"derivedFrom":sQuery(id+"F0.wireOp",EDGE,"E86.0")}),1.0]])]});
            var Q5;
            Q5=makeQuery(id+"F0.imprint","IMPRINT",FACE,{"disambiguationData":[TD([[makeQuery(id+"F0.imprint","IMPRINT",EDGE,{"derivedFrom":sQuery(id+"F0.wireOp",EDGE,"E80.0")}),1.0]])]});
            var Q6;
            Q6=makeQuery(id+"F0.imprint","IMPRINT",FACE,{"disambiguationData":[TD([[makeQuery(id+"F0.imprint","IMPRINT",EDGE,{"derivedFrom":sQuery(id+"F0.wireOp",EDGE,"E78.0")}),1.0]])]});
            var Q7;
            Q7=makeQuery(id+"F0.imprint","IMPRINT",FACE,{"disambiguationData":[TD([[makeQuery(id+"F0.imprint","IMPRINT",EDGE,{"derivedFrom":sQuery(id+"F0.wireOp",EDGE,"E76.0")}),1.0]])]});
            var Q8;
            Q8=makeQuery(id+"F0.imprint","IMPRINT",FACE,{"disambiguationData":[TD([[makeQuery(id+"F0.imprint","IMPRINT",EDGE,{"derivedFrom":sQuery(id+"F0.wireOp",EDGE,"E128.MirrorCS")}),1.0]])]});
            var Q9;
            Q9=makeQuery(id+"F0.imprint","IMPRINT",FACE,{"disambiguationData":[TD([[makeQuery(id+"F0.imprint","IMPRINT",EDGE,{"derivedFrom":sQuery(id+"F0.wireOp",EDGE,"E125.MirrorCS")}),1.0]])]});
            var Q10;
            Q10=makeQuery(id+"F0.imprint","IMPRINT",FACE,{"disambiguationData":[TD([[makeQuery(id+"F0.imprint","IMPRINT",EDGE,{"derivedFrom":sQuery(id+"F0.wireOp",EDGE,"E120.MirrorCS")}),1.0]])]});
            var Q11;
            Q11=makeQuery(id+"F0.imprint","IMPRINT",FACE,{"disambiguationData":[TD([[makeQuery(id+"F0.imprint","IMPRINT",EDGE,{"derivedFrom":sQuery(id+"F0.wireOp",EDGE,"E121.MirrorCS")}),1.0]])]});
            var Q12;
            Q12=makeQuery(id+"F0.imprint","IMPRINT",FACE,{"disambiguationData":[TD([[makeQuery(id+"F0.imprint","IMPRINT",EDGE,{"derivedFrom":sQuery(id+"F0.wireOp",EDGE,"E123.MirrorCS")}),1.0]])]});
            var Q13;
            Q13=makeQuery(id+"F0.imprint","IMPRINT",FACE,{"disambiguationData":[TD([[makeQuery(id+"F0.imprint","IMPRINT",EDGE,{"derivedFrom":sQuery(id+"F0.wireOp",EDGE,"E124.MirrorCS")}),1.0]])]});
            var Q14;
            Q14=makeQuery(id+"F0.imprint","IMPRINT",FACE,{"disambiguationData":[TD([[makeQuery(id+"F0.imprint","IMPRINT",EDGE,{"derivedFrom":sQuery(id+"F0.wireOp",EDGE,"E127.MirrorCS")}),1.0]])]});
            var Q15;
            Q15=makeQuery(id+"F0.imprint","IMPRINT",FACE,{"disambiguationData":[TD([[makeQuery(id+"F0.imprint","IMPRINT",EDGE,{"derivedFrom":sQuery(id+"F0.wireOp",EDGE,"E126.MirrorCS")}),1.0]])]});
            extrude(context, id + "F14", {"entities" : qUnion([Q0, Q1, Q2, Q3, Q4, Q5, Q6, Q7, Q8, Q9, Q10, Q11, Q12, Q13, Q14, Q15]), "depth" : 1.27 * mm});
        }
        {
            var Q0;
            Q0=makeQuery(id+"F0.imprint","IMPRINT",FACE,{"disambiguationData":[TD([[makeQuery(id+"F0.imprint","IMPRINT",EDGE,{"derivedFrom":sQuery(id+"F0.wireOp",EDGE,"E73.0")}),-1.0]])]});
            var Q1;
            Q1=makeQuery(id+"F0.imprint","IMPRINT",FACE,{"disambiguationData":[TD([[makeQuery(id+"F0.imprint","IMPRINT",EDGE,{"derivedFrom":sQuery(id+"F0.wireOp",EDGE,"E75.0")}),1.0]])]});
            var Q2;
            Q2=makeQuery(id+"F0.imprint","IMPRINT",FACE,{"disambiguationData":[TD([[makeQuery(id+"F0.imprint","IMPRINT",EDGE,{"derivedFrom":sQuery(id+"F0.wireOp",EDGE,"E83.0")}),1.0]])]});
            var Q3;
            Q3=makeQuery(id+"F0.imprint","IMPRINT",FACE,{"disambiguationData":[TD([[makeQuery(id+"F0.imprint","IMPRINT",EDGE,{"derivedFrom":sQuery(id+"F0.wireOp",EDGE,"E85.0")}),-1.0]])]});
            var Q4;
            Q4=makeQuery(id+"F0.imprint","IMPRINT",FACE,{"disambiguationData":[TD([[makeQuery(id+"F0.imprint","IMPRINT",EDGE,{"derivedFrom":sQuery(id+"F0.wireOp",EDGE,"E87.0")}),1.0]])]});
            var Q5;
            Q5=makeQuery(id+"F0.imprint","IMPRINT",FACE,{"disambiguationData":[TD([[makeQuery(id+"F0.imprint","IMPRINT",EDGE,{"derivedFrom":sQuery(id+"F0.wireOp",EDGE,"E81.0")}),1.0]])]});
            var Q6;
            Q6=makeQuery(id+"F0.imprint","IMPRINT",FACE,{"disambiguationData":[TD([[makeQuery(id+"F0.imprint","IMPRINT",EDGE,{"derivedFrom":sQuery(id+"F0.wireOp",EDGE,"E79.0")}),1.0]])]});
            var Q7;
            Q7=makeQuery(id+"F0.imprint","IMPRINT",FACE,{"disambiguationData":[TD([[makeQuery(id+"F0.imprint","IMPRINT",EDGE,{"derivedFrom":sQuery(id+"F0.wireOp",EDGE,"E77.0")}),1.0]])]});
            var Q8;
            Q8=makeQuery(id+"F0.imprint","IMPRINT",FACE,{"disambiguationData":[TD([[makeQuery(id+"F0.imprint","IMPRINT",EDGE,{"derivedFrom":sQuery(id+"F0.wireOp",EDGE,"E130.MirrorCS")}),-1.0]])]});
            var Q9;
            Q9=makeQuery(id+"F0.imprint","IMPRINT",FACE,{"disambiguationData":[TD([[makeQuery(id+"F0.imprint","IMPRINT",EDGE,{"derivedFrom":sQuery(id+"F0.wireOp",EDGE,"E129.MirrorCS")}),-1.0]])]});
            var Q10;
            Q10=makeQuery(id+"F0.imprint","IMPRINT",FACE,{"disambiguationData":[TD([[makeQuery(id+"F0.imprint","IMPRINT",EDGE,{"derivedFrom":sQuery(id+"F0.wireOp",EDGE,"E132.MirrorCS")}),-1.0]])]});
            var Q11;
            Q11=makeQuery(id+"F0.imprint","IMPRINT",FACE,{"disambiguationData":[TD([[makeQuery(id+"F0.imprint","IMPRINT",EDGE,{"derivedFrom":sQuery(id+"F0.wireOp",EDGE,"E131.MirrorCS")}),1.0]])]});
            var Q12;
            Q12=makeQuery(id+"F0.imprint","IMPRINT",FACE,{"disambiguationData":[TD([[makeQuery(id+"F0.imprint","IMPRINT",EDGE,{"derivedFrom":sQuery(id+"F0.wireOp",EDGE,"E144.MirrorCS")}),1.0]])]});
            var Q13;
            Q13=makeQuery(id+"F0.imprint","IMPRINT",FACE,{"disambiguationData":[TD([[makeQuery(id+"F0.imprint","IMPRINT",EDGE,{"derivedFrom":sQuery(id+"F0.wireOp",EDGE,"E154.MirrorCS")}),-1.0]])]});
            var Q14;
            Q14=makeQuery(id+"F0.imprint","IMPRINT",FACE,{"disambiguationData":[TD([[makeQuery(id+"F0.imprint","IMPRINT",EDGE,{"derivedFrom":sQuery(id+"F0.wireOp",EDGE,"E133.MirrorCS")}),-1.0]])]});
            var Q15;
            Q15=makeQuery(id+"F0.imprint","IMPRINT",FACE,{"disambiguationData":[TD([[makeQuery(id+"F0.imprint","IMPRINT",EDGE,{"derivedFrom":sQuery(id+"F0.wireOp",EDGE,"E134.MirrorCS")}),-1.0]])]});
            extrude(context, id + "F15", {"entities" : qUnion([Q0, Q1, Q2, Q3, Q4, Q5, Q6, Q7, Q8, Q9, Q10, Q11, Q12, Q13, Q14, Q15]), "depth" : 1.27 * mm});
        }
        {
            var Q0;
            Q0=makeQuery(id+"F14.opExtrude","CAP_FACE",FACE,{"disambiguationData":[OSD([sQuery(id+"F0.wireOp",EDGE,"E72.0"),sQuery(id+"F0.wireOp",EDGE,"E72.1"),sQuery(id+"F0.wireOp",EDGE,"E72.2"),sQuery(id+"F0.wireOp",EDGE,"E72.3"),sQuery(id+"F0.wireOp",EDGE,"E73.0"),sQuery(id+"F0.wireOp",EDGE,"E73.1"),sQuery(id+"F0.wireOp",EDGE,"E73.2")])],"isStart":false});
            var Q1;
            Q1=makeQuery(id+"F14.opExtrude","CAP_FACE",FACE,{"disambiguationData":[OSD([sQuery(id+"F0.wireOp",EDGE,"E74.0"),sQuery(id+"F0.wireOp",EDGE,"E74.1"),sQuery(id+"F0.wireOp",EDGE,"E74.2"),sQuery(id+"F0.wireOp",EDGE,"E74.3"),sQuery(id+"F0.wireOp",EDGE,"E75.0"),sQuery(id+"F0.wireOp",EDGE,"E75.1"),sQuery(id+"F0.wireOp",EDGE,"E75.2")])],"isStart":false});
            var Q2;
            Q2=makeQuery(id+"F14.opExtrude","CAP_FACE",FACE,{"disambiguationData":[OSD([sQuery(id+"F0.wireOp",EDGE,"E82.0"),sQuery(id+"F0.wireOp",EDGE,"E82.1"),sQuery(id+"F0.wireOp",EDGE,"E82.2"),sQuery(id+"F0.wireOp",EDGE,"E82.3"),sQuery(id+"F0.wireOp",EDGE,"E83.0"),sQuery(id+"F0.wireOp",EDGE,"E83.1"),sQuery(id+"F0.wireOp",EDGE,"E83.2")])],"isStart":false});
            var Q3;
            Q3=makeQuery(id+"F14.opExtrude","CAP_FACE",FACE,{"disambiguationData":[OSD([sQuery(id+"F0.wireOp",EDGE,"E84.0"),sQuery(id+"F0.wireOp",EDGE,"E84.1"),sQuery(id+"F0.wireOp",EDGE,"E84.2"),sQuery(id+"F0.wireOp",EDGE,"E84.3"),sQuery(id+"F0.wireOp",EDGE,"E85.0"),sQuery(id+"F0.wireOp",EDGE,"E85.1"),sQuery(id+"F0.wireOp",EDGE,"E85.2")])],"isStart":false});
            var Q4;
            Q4=makeQuery(id+"F14.opExtrude","CAP_FACE",FACE,{"disambiguationData":[OSD([sQuery(id+"F0.wireOp",EDGE,"E86.0"),sQuery(id+"F0.wireOp",EDGE,"E86.1"),sQuery(id+"F0.wireOp",EDGE,"E86.2"),sQuery(id+"F0.wireOp",EDGE,"E86.3"),sQuery(id+"F0.wireOp",EDGE,"E87.0"),sQuery(id+"F0.wireOp",EDGE,"E87.1"),sQuery(id+"F0.wireOp",EDGE,"E87.2")])],"isStart":false});
            var Q5;
            Q5=makeQuery(id+"F14.opExtrude","CAP_FACE",FACE,{"disambiguationData":[OSD([sQuery(id+"F0.wireOp",EDGE,"E80.0"),sQuery(id+"F0.wireOp",EDGE,"E80.1"),sQuery(id+"F0.wireOp",EDGE,"E80.2"),sQuery(id+"F0.wireOp",EDGE,"E80.3"),sQuery(id+"F0.wireOp",EDGE,"E81.0"),sQuery(id+"F0.wireOp",EDGE,"E81.1"),sQuery(id+"F0.wireOp",EDGE,"E81.2")])],"isStart":false});
            var Q6;
            Q6=makeQuery(id+"F14.opExtrude","CAP_FACE",FACE,{"disambiguationData":[OSD([sQuery(id+"F0.wireOp",EDGE,"E78.0"),sQuery(id+"F0.wireOp",EDGE,"E78.1"),sQuery(id+"F0.wireOp",EDGE,"E78.2"),sQuery(id+"F0.wireOp",EDGE,"E78.3"),sQuery(id+"F0.wireOp",EDGE,"E79.0"),sQuery(id+"F0.wireOp",EDGE,"E79.1"),sQuery(id+"F0.wireOp",EDGE,"E79.2")])],"isStart":false});
            var Q7;
            Q7=makeQuery(id+"F14.opExtrude","CAP_FACE",FACE,{"disambiguationData":[OSD([sQuery(id+"F0.wireOp",EDGE,"E76.0"),sQuery(id+"F0.wireOp",EDGE,"E76.1"),sQuery(id+"F0.wireOp",EDGE,"E76.2"),sQuery(id+"F0.wireOp",EDGE,"E76.3"),sQuery(id+"F0.wireOp",EDGE,"E77.0"),sQuery(id+"F0.wireOp",EDGE,"E77.1"),sQuery(id+"F0.wireOp",EDGE,"E77.2")])],"isStart":false});
            var Q8;
            Q8=makeQuery(id+"F14.opExtrude","CAP_FACE",FACE,{"disambiguationData":[OSD([sQuery(id+"F0.wireOp",EDGE,"E128.MirrorCS"),sQuery(id+"F0.wireOp",EDGE,"E129.MirrorCS"),sQuery(id+"F0.wireOp",EDGE,"E143.MirrorCS"),sQuery(id+"F0.wireOp",EDGE,"E160.MirrorCS"),sQuery(id+"F0.wireOp",EDGE,"E164.MirrorCS"),sQuery(id+"F0.wireOp",EDGE,"E166.MirrorCS"),sQuery(id+"F0.wireOp",EDGE,"E172.MirrorCS")])],"isStart":false});
            var Q9;
            Q9=makeQuery(id+"F14.opExtrude","CAP_FACE",FACE,{"disambiguationData":[OSD([sQuery(id+"F0.wireOp",EDGE,"E126.MirrorCS"),sQuery(id+"F0.wireOp",EDGE,"E132.MirrorCS"),sQuery(id+"F0.wireOp",EDGE,"E138.MirrorCS"),sQuery(id+"F0.wireOp",EDGE,"E150.MirrorCS"),sQuery(id+"F0.wireOp",EDGE,"E168.MirrorCS"),sQuery(id+"F0.wireOp",EDGE,"E176.MirrorCS"),sQuery(id+"F0.wireOp",EDGE,"E192.MirrorCS")])],"isStart":false});
            var Q10;
            Q10=makeQuery(id+"F14.opExtrude","CAP_FACE",FACE,{"disambiguationData":[OSD([sQuery(id+"F0.wireOp",EDGE,"E127.MirrorCS"),sQuery(id+"F0.wireOp",EDGE,"E131.MirrorCS"),sQuery(id+"F0.wireOp",EDGE,"E135.MirrorCS"),sQuery(id+"F0.wireOp",EDGE,"E142.MirrorCS"),sQuery(id+"F0.wireOp",EDGE,"E145.MirrorCS"),sQuery(id+"F0.wireOp",EDGE,"E163.MirrorCS"),sQuery(id+"F0.wireOp",EDGE,"E177.MirrorCS")])],"isStart":false});
            var Q11;
            Q11=makeQuery(id+"F14.opExtrude","CAP_FACE",FACE,{"disambiguationData":[OSD([sQuery(id+"F0.wireOp",EDGE,"E124.MirrorCS"),sQuery(id+"F0.wireOp",EDGE,"E139.MirrorCS"),sQuery(id+"F0.wireOp",EDGE,"E144.MirrorCS"),sQuery(id+"F0.wireOp",EDGE,"E157.MirrorCS"),sQuery(id+"F0.wireOp",EDGE,"E169.MirrorCS"),sQuery(id+"F0.wireOp",EDGE,"E179.MirrorCS"),sQuery(id+"F0.wireOp",EDGE,"E193.MirrorCS")])],"isStart":false});
            var Q12;
            Q12=makeQuery(id+"F14.opExtrude","CAP_FACE",FACE,{"disambiguationData":[OSD([sQuery(id+"F0.wireOp",EDGE,"E123.MirrorCS"),sQuery(id+"F0.wireOp",EDGE,"E136.MirrorCS"),sQuery(id+"F0.wireOp",EDGE,"E149.MirrorCS"),sQuery(id+"F0.wireOp",EDGE,"E154.MirrorCS"),sQuery(id+"F0.wireOp",EDGE,"E175.MirrorCS"),sQuery(id+"F0.wireOp",EDGE,"E184.MirrorCS"),sQuery(id+"F0.wireOp",EDGE,"E187.MirrorCS")])],"isStart":false});
            var Q13;
            Q13=makeQuery(id+"F14.opExtrude","CAP_FACE",FACE,{"disambiguationData":[OSD([sQuery(id+"F0.wireOp",EDGE,"E121.MirrorCS"),sQuery(id+"F0.wireOp",EDGE,"E133.MirrorCS"),sQuery(id+"F0.wireOp",EDGE,"E147.MirrorCS"),sQuery(id+"F0.wireOp",EDGE,"E156.MirrorCS"),sQuery(id+"F0.wireOp",EDGE,"E158.MirrorCS"),sQuery(id+"F0.wireOp",EDGE,"E178.MirrorCS"),sQuery(id+"F0.wireOp",EDGE,"E190.MirrorCS")])],"isStart":false});
            var Q14;
            Q14=makeQuery(id+"F14.opExtrude","CAP_FACE",FACE,{"disambiguationData":[OSD([sQuery(id+"F0.wireOp",EDGE,"E120.MirrorCS"),sQuery(id+"F0.wireOp",EDGE,"E134.MirrorCS"),sQuery(id+"F0.wireOp",EDGE,"E140.MirrorCS"),sQuery(id+"F0.wireOp",EDGE,"E159.MirrorCS"),sQuery(id+"F0.wireOp",EDGE,"E162.MirrorCS"),sQuery(id+"F0.wireOp",EDGE,"E165.MirrorCS"),sQuery(id+"F0.wireOp",EDGE,"E195.MirrorCS")])],"isStart":false});
            var Q15;
            Q15=makeQuery(id+"F14.opExtrude","CAP_FACE",FACE,{"disambiguationData":[OSD([sQuery(id+"F0.wireOp",EDGE,"E125.MirrorCS"),sQuery(id+"F0.wireOp",EDGE,"E130.MirrorCS"),sQuery(id+"F0.wireOp",EDGE,"E137.MirrorCS"),sQuery(id+"F0.wireOp",EDGE,"E146.MirrorCS"),sQuery(id+"F0.wireOp",EDGE,"E152.MirrorCS"),sQuery(id+"F0.wireOp",EDGE,"E155.MirrorCS"),sQuery(id+"F0.wireOp",EDGE,"E161.MirrorCS")])],"isStart":false});
            fillet(context, id + "F16", {"entities" : qUnion([Q0, Q1, Q2, Q3, Q4, Q5, Q6, Q7, Q8, Q9, Q10, Q11, Q12, Q13, Q14, Q15]), "radius" : 0.5 * mm, "tangentPropagation" : true, "allowEdgeOverflow" : false});
        }
        {
            var Q0;
            Q0=makeQuery(id+"F15.opExtrude","CAP_FACE",FACE,{"disambiguationData":[OSD([sQuery(id+"F0.wireOp",EDGE,"E73.0"),sQuery(id+"F0.wireOp",EDGE,"E73.1"),sQuery(id+"F0.wireOp",EDGE,"E73.2")])],"isStart":false});
            var Q1;
            Q1=makeQuery(id+"F15.opExtrude","CAP_FACE",FACE,{"disambiguationData":[OSD([sQuery(id+"F0.wireOp",EDGE,"E75.0"),sQuery(id+"F0.wireOp",EDGE,"E75.1"),sQuery(id+"F0.wireOp",EDGE,"E75.2")])],"isStart":false});
            var Q2;
            Q2=makeQuery(id+"F15.opExtrude","CAP_FACE",FACE,{"disambiguationData":[OSD([sQuery(id+"F0.wireOp",EDGE,"E83.0"),sQuery(id+"F0.wireOp",EDGE,"E83.1"),sQuery(id+"F0.wireOp",EDGE,"E83.2")])],"isStart":false});
            var Q3;
            Q3=makeQuery(id+"F15.opExtrude","CAP_FACE",FACE,{"disambiguationData":[OSD([sQuery(id+"F0.wireOp",EDGE,"E77.0"),sQuery(id+"F0.wireOp",EDGE,"E77.1"),sQuery(id+"F0.wireOp",EDGE,"E77.2")])],"isStart":false});
            var Q4;
            Q4=makeQuery(id+"F15.opExtrude","CAP_FACE",FACE,{"disambiguationData":[OSD([sQuery(id+"F0.wireOp",EDGE,"E79.0"),sQuery(id+"F0.wireOp",EDGE,"E79.1"),sQuery(id+"F0.wireOp",EDGE,"E79.2")])],"isStart":false});
            var Q5;
            Q5=makeQuery(id+"F15.opExtrude","CAP_FACE",FACE,{"disambiguationData":[OSD([sQuery(id+"F0.wireOp",EDGE,"E81.0"),sQuery(id+"F0.wireOp",EDGE,"E81.1"),sQuery(id+"F0.wireOp",EDGE,"E81.2")])],"isStart":false});
            var Q6;
            Q6=makeQuery(id+"F15.opExtrude","CAP_FACE",FACE,{"disambiguationData":[OSD([sQuery(id+"F0.wireOp",EDGE,"E87.0"),sQuery(id+"F0.wireOp",EDGE,"E87.1"),sQuery(id+"F0.wireOp",EDGE,"E87.2")])],"isStart":false});
            var Q7;
            Q7=makeQuery(id+"F15.opExtrude","CAP_FACE",FACE,{"disambiguationData":[OSD([sQuery(id+"F0.wireOp",EDGE,"E85.0"),sQuery(id+"F0.wireOp",EDGE,"E85.1"),sQuery(id+"F0.wireOp",EDGE,"E85.2")])],"isStart":false});
            var Q8;
            Q8=makeQuery(id+"F15.opExtrude","CAP_FACE",FACE,{"disambiguationData":[OSD([sQuery(id+"F0.wireOp",EDGE,"E130.MirrorCS"),sQuery(id+"F0.wireOp",EDGE,"E146.MirrorCS"),sQuery(id+"F0.wireOp",EDGE,"E161.MirrorCS")])],"isStart":false});
            var Q9;
            Q9=makeQuery(id+"F15.opExtrude","CAP_FACE",FACE,{"disambiguationData":[OSD([sQuery(id+"F0.wireOp",EDGE,"E129.MirrorCS"),sQuery(id+"F0.wireOp",EDGE,"E160.MirrorCS"),sQuery(id+"F0.wireOp",EDGE,"E164.MirrorCS")])],"isStart":false});
            var Q10;
            Q10=makeQuery(id+"F15.opExtrude","CAP_FACE",FACE,{"disambiguationData":[OSD([sQuery(id+"F0.wireOp",EDGE,"E132.MirrorCS"),sQuery(id+"F0.wireOp",EDGE,"E138.MirrorCS"),sQuery(id+"F0.wireOp",EDGE,"E176.MirrorCS")])],"isStart":false});
            var Q11;
            Q11=makeQuery(id+"F15.opExtrude","CAP_FACE",FACE,{"disambiguationData":[OSD([sQuery(id+"F0.wireOp",EDGE,"E131.MirrorCS"),sQuery(id+"F0.wireOp",EDGE,"E135.MirrorCS"),sQuery(id+"F0.wireOp",EDGE,"E142.MirrorCS")])],"isStart":false});
            var Q12;
            Q12=makeQuery(id+"F15.opExtrude","CAP_FACE",FACE,{"disambiguationData":[OSD([sQuery(id+"F0.wireOp",EDGE,"E144.MirrorCS"),sQuery(id+"F0.wireOp",EDGE,"E169.MirrorCS"),sQuery(id+"F0.wireOp",EDGE,"E179.MirrorCS")])],"isStart":false});
            var Q13;
            Q13=makeQuery(id+"F15.opExtrude","CAP_FACE",FACE,{"disambiguationData":[OSD([sQuery(id+"F0.wireOp",EDGE,"E154.MirrorCS"),sQuery(id+"F0.wireOp",EDGE,"E175.MirrorCS"),sQuery(id+"F0.wireOp",EDGE,"E187.MirrorCS")])],"isStart":false});
            var Q14;
            Q14=makeQuery(id+"F15.opExtrude","CAP_FACE",FACE,{"disambiguationData":[OSD([sQuery(id+"F0.wireOp",EDGE,"E133.MirrorCS"),sQuery(id+"F0.wireOp",EDGE,"E178.MirrorCS"),sQuery(id+"F0.wireOp",EDGE,"E190.MirrorCS")])],"isStart":false});
            var Q15;
            Q15=makeQuery(id+"F15.opExtrude","CAP_FACE",FACE,{"disambiguationData":[OSD([sQuery(id+"F0.wireOp",EDGE,"E134.MirrorCS"),sQuery(id+"F0.wireOp",EDGE,"E159.MirrorCS"),sQuery(id+"F0.wireOp",EDGE,"E165.MirrorCS")])],"isStart":false});
            fillet(context, id + "F17", {"entities" : qUnion([Q0, Q1, Q2, Q3, Q4, Q5, Q6, Q7, Q8, Q9, Q10, Q11, Q12, Q13, Q14, Q15]), "radius" : 0.5 * mm, "tangentPropagation" : true, "allowEdgeOverflow" : false});
        }
        {
            var Q0;
            Q0=makeQuery(id+"F0.imprint","IMPRINT",FACE,{"disambiguationData":[TD([[makeQuery(id+"F0.imprint","IMPRINT",EDGE,{"derivedFrom":sQuery(id+"F0.wireOp",EDGE,"E49")}),-1.0]])]});
            var Q1;
            Q1=makeQuery(id+"F0.imprint","IMPRINT",FACE,{"disambiguationData":[TD([[makeQuery(id+"F0.imprint","IMPRINT",EDGE,{"derivedFrom":sQuery(id+"F0.wireOp",EDGE,"E2")}),-1.0]])]});
            var Q2;
            Q2=makeQuery(id+"F0.imprint","IMPRINT",FACE,{"disambiguationData":[TD([[makeQuery(id+"F0.imprint","IMPRINT",EDGE,{"derivedFrom":sQuery(id+"F0.wireOp",EDGE,"E37")}),1.0]])]});
            var Q3;
            Q3=makeQuery(id+"F0.imprint","IMPRINT",FACE,{"disambiguationData":[TD([[makeQuery(id+"F0.imprint","IMPRINT",EDGE,{"derivedFrom":sQuery(id+"F0.wireOp",EDGE,"E46")}),-1.0]])]});
            extrude(context, id + "F18", {"entities" : qUnion([Q0, Q1, Q2, Q3]), "depth" : 1.27 * mm});
        }
        {
            var Q0;
            {var subQ1=sQuery(id+"F0.wireOp",EDGE,"E41");Q0=makeQuery(id+"F0.imprint","IMPRINT",FACE,{"disambiguationData":[TD([[makeQuery(id+"F0.imprint","IMPRINT",EDGE,{"derivedFrom":subQ1}),1.0]])]});}
            var Q1;
            {var subQ1=sQuery(id+"F0.wireOp",EDGE,"E38");Q1=makeQuery(id+"F0.imprint","IMPRINT",FACE,{"disambiguationData":[TD([[makeQuery(id+"F0.imprint","IMPRINT",EDGE,{"derivedFrom":subQ1}),1.0]])]});}
            var Q2;
            {var subQ1=sQuery(id+"F0.wireOp",EDGE,"E37");Q2=makeQuery(id+"F0.imprint","IMPRINT",FACE,{"disambiguationData":[TD([[makeQuery(id+"F0.imprint","IMPRINT",EDGE,{"derivedFrom":subQ1}),-1.0]])]});}
            var Q3;
            {var subQ2=sQuery(id+"F0.wireOp",EDGE,"E48");Q3=makeQuery(id+"F0.imprint","IMPRINT",FACE,{"disambiguationData":[TD([[makeQuery(id+"F0.imprint","IMPRINT",EDGE,{"derivedFrom":subQ2}),1.0]])]});}
            extrude(context, id + "F19", {"entities" : qUnion([Q0, Q1, Q2, Q3]), "depth" : 1.27 * mm});
        }
        {
            var Q0;
            Q0=makeQuery(id+"F19.opExtrude","CAP_FACE",FACE,{"disambiguationData":[OSD([sQuery(id+"F0.wireOp",EDGE,"E48"),sQuery(id+"F0.wireOp",EDGE,"E49"),sQuery(id+"F0.wireOp",EDGE,"JD9rd0Fr-nhDj-zQhR-adwM-q48NUqkORWYs"),sQuery(id+"F0.wireOp",EDGE,"E55")])],"isStart":false});
            var Q1;
            Q1=makeQuery(id+"F19.opExtrude","CAP_FACE",FACE,{"disambiguationData":[OSD([sQuery(id+"F0.wireOp",EDGE,"E41"),sQuery(id+"F0.wireOp",EDGE,"E51"),sQuery(id+"F0.wireOp",EDGE,"E53"),sQuery(id+"F0.wireOp",EDGE,"E54")])],"isStart":false});
            var Q2;
            Q2=makeQuery(id+"F19.opExtrude","CAP_FACE",FACE,{"disambiguationData":[OSD([sQuery(id+"F0.wireOp",EDGE,"E38"),sQuery(id+"F0.wireOp",EDGE,"E43"),sQuery(id+"F0.wireOp",EDGE,"E44"),sQuery(id+"F0.wireOp",EDGE,"E45")])],"isStart":false});
            var Q3;
            Q3=makeQuery(id+"F19.opExtrude","CAP_FACE",FACE,{"disambiguationData":[OSD([sQuery(id+"F0.wireOp",EDGE,"E37"),sQuery(id+"F0.wireOp",EDGE,"E46"),sQuery(id+"F0.wireOp",EDGE,"E52"),sQuery(id+"F0.wireOp",EDGE,"Iv0IE3YL-SCPa-R002-ozm4-uklGqbIbVbpd")])],"isStart":false});
            fillet(context, id + "F20", {"entities" : qUnion([Q0, Q1, Q2, Q3]), "radius" : 0.5 * mm, "tangentPropagation" : true, "allowEdgeOverflow" : false});
        }
        {
            var Q0;
            Q0=makeQuery(id+"F18.opExtrude","CAP_FACE",FACE,{"disambiguationData":[OSD([sQuery(id+"F0.wireOp",EDGE,"E46"),sQuery(id+"F0.wireOp",EDGE,"E47"),sQuery(id+"F0.wireOp",EDGE,"E0"),sQuery(id+"F0.wireOp",EDGE,"E48")])],"isStart":false});
            var Q1;
            Q1=makeQuery(id+"F18.opExtrude","CAP_FACE",FACE,{"disambiguationData":[OSD([sQuery(id+"F0.wireOp",EDGE,"E37"),sQuery(id+"F0.wireOp",EDGE,"E38"),sQuery(id+"F0.wireOp",EDGE,"E39"),sQuery(id+"F0.wireOp",EDGE,"E40")])],"isStart":false});
            var Q2;
            Q2=makeQuery(id+"F18.opExtrude","CAP_FACE",FACE,{"disambiguationData":[OSD([sQuery(id+"F0.wireOp",EDGE,"E2"),sQuery(id+"F0.wireOp",EDGE,"E41"),sQuery(id+"F0.wireOp",EDGE,"E42"),sQuery(id+"F0.wireOp",EDGE,"E43")])],"isStart":false});
            var Q3;
            Q3=makeQuery(id+"F18.opExtrude","CAP_FACE",FACE,{"disambiguationData":[OSD([sQuery(id+"F0.wireOp",EDGE,"E49"),sQuery(id+"F0.wireOp",EDGE,"E1"),sQuery(id+"F0.wireOp",EDGE,"E50"),sQuery(id+"F0.wireOp",EDGE,"E51")])],"isStart":false});
            fillet(context, id + "F21", {"entities" : qUnion([Q0, Q1, Q2, Q3]), "radius" : 0.5 * mm, "tangentPropagation" : true, "allowEdgeOverflow" : false});
        }
        {
            var Q0;
            Q0=makeQuery(id+"F0.imprint","IMPRINT",FACE,{"disambiguationData":[TD([[makeQuery(id+"F0.imprint","IMPRINT",EDGE,{"derivedFrom":sQuery(id+"F0.wireOp",EDGE,"039e5912-03fe-4849-a1df-3fe704ae40270.MirrorCS")}),-1.0]])]});
            var Q1;
            Q1=makeQuery(id+"F0.imprint","IMPRINT",FACE,{"disambiguationData":[TD([[makeQuery(id+"F0.imprint","IMPRINT",EDGE,{"derivedFrom":sQuery(id+"F0.wireOp",EDGE,"c6d78a54-423a-4be5-bd58-37ad933318d30.MirrorCS")}),1.0]])]});
            var Q2;
            Q2=makeQuery(id+"F0.imprint","IMPRINT",FACE,{"disambiguationData":[TD([[makeQuery(id+"F0.imprint","IMPRINT",EDGE,{"derivedFrom":sQuery(id+"F0.wireOp",EDGE,"E218.MirrorCS")}),1.0]])]});
            var Q3;
            Q3=makeQuery(id+"F0.imprint","IMPRINT",FACE,{"disambiguationData":[TD([[makeQuery(id+"F0.imprint","IMPRINT",EDGE,{"derivedFrom":sQuery(id+"F0.wireOp",EDGE,"E220.MirrorCS")}),1.0]])]});
            var Q4;
            Q4=makeQuery(id+"F0.imprint","IMPRINT",FACE,{"disambiguationData":[TD([[makeQuery(id+"F0.imprint","IMPRINT",EDGE,{"derivedFrom":sQuery(id+"F0.wireOp",EDGE,"8a471478-5bdd-42e6-9c6a-fa3cf6a126bb0.MirrorCS")}),-1.0]])]});
            var Q5;
            Q5=makeQuery(id+"F0.imprint","IMPRINT",FACE,{"disambiguationData":[TD([[makeQuery(id+"F0.imprint","IMPRINT",EDGE,{"derivedFrom":sQuery(id+"F0.wireOp",EDGE,"76a2c5d4-d9ba-405b-a4bd-bbbd33ab3d290.MirrorCS")}),1.0]])]});
            var Q6;
            Q6=makeQuery(id+"F0.imprint","IMPRINT",FACE,{"disambiguationData":[TD([[makeQuery(id+"F0.imprint","IMPRINT",EDGE,{"derivedFrom":sQuery(id+"F0.wireOp",EDGE,"E222.MirrorCS")}),1.0]])]});
            var Q7;
            Q7=makeQuery(id+"F0.imprint","IMPRINT",FACE,{"disambiguationData":[TD([[makeQuery(id+"F0.imprint","IMPRINT",EDGE,{"derivedFrom":sQuery(id+"F0.wireOp",EDGE,"f2dac46b-1d41-4af4-91b8-a348f944510e0.MirrorCS")}),1.0]])]});
            var Q8;
            Q8=makeQuery(id+"F0.imprint","IMPRINT",FACE,{"disambiguationData":[TD([[makeQuery(id+"F0.imprint","IMPRINT",EDGE,{"derivedFrom":sQuery(id+"F0.wireOp",EDGE,"E216.MirrorCS")}),-1.0]])]});
            var Q9;
            Q9=makeQuery(id+"F0.imprint","IMPRINT",FACE,{"disambiguationData":[TD([[makeQuery(id+"F0.imprint","IMPRINT",EDGE,{"derivedFrom":sQuery(id+"F0.wireOp",EDGE,"E215.0")}),1.0]])]});
            var Q10;
            Q10=makeQuery(id+"F0.imprint","IMPRINT",FACE,{"disambiguationData":[TD([[makeQuery(id+"F0.imprint","IMPRINT",EDGE,{"derivedFrom":sQuery(id+"F0.wireOp",EDGE,"ab5a4bc4-6390-41e3-ba40-baced2ec88170.MirrorCS")}),-1.0]])]});
            var Q11;
            Q11=makeQuery(id+"F0.imprint","IMPRINT",FACE,{"disambiguationData":[TD([[makeQuery(id+"F0.imprint","IMPRINT",EDGE,{"derivedFrom":sQuery(id+"F0.wireOp",EDGE,"b78252e9-c6d8-4dbf-b09c-8e9b2fdb4f300.MirrorCS")}),1.0]])]});
            var Q12;
            Q12=makeQuery(id+"F0.imprint","IMPRINT",FACE,{"disambiguationData":[TD([[makeQuery(id+"F0.imprint","IMPRINT",EDGE,{"derivedFrom":sQuery(id+"F0.wireOp",EDGE,"E212.0")}),-1.0]])]});
            var Q13;
            Q13=makeQuery(id+"F0.imprint","IMPRINT",FACE,{"disambiguationData":[TD([[makeQuery(id+"F0.imprint","IMPRINT",EDGE,{"derivedFrom":sQuery(id+"F0.wireOp",EDGE,"E213.0")}),-1.0]])]});
            var Q14;
            Q14=makeQuery(id+"F0.imprint","IMPRINT",FACE,{"disambiguationData":[TD([[makeQuery(id+"F0.imprint","IMPRINT",EDGE,{"derivedFrom":sQuery(id+"F0.wireOp",EDGE,"4b1ba489-c2c9-461b-8f57-ccbc949286b8.0")}),1.0]])]});
            var Q15;
            Q15=makeQuery(id+"F0.imprint","IMPRINT",FACE,{"disambiguationData":[TD([[makeQuery(id+"F0.imprint","IMPRINT",EDGE,{"derivedFrom":sQuery(id+"F0.wireOp",EDGE,"78d50b2d-89b1-49a9-bfa7-751a130da7ff0.MirrorCS")}),-1.0]])]});
            var Q16;
            Q16=makeQuery(id+"F0.imprint","IMPRINT",FACE,{"disambiguationData":[TD([[makeQuery(id+"F0.imprint","IMPRINT",EDGE,{"derivedFrom":sQuery(id+"F0.wireOp",EDGE,"E214.0")}),-1.0]])]});
            var Q17;
            Q17=makeQuery(id+"F0.imprint","IMPRINT",FACE,{"disambiguationData":[TD([[makeQuery(id+"F0.imprint","IMPRINT",EDGE,{"derivedFrom":sQuery(id+"F0.wireOp",EDGE,"E230.0")}),1.0]])]});
            var Q18;
            Q18=makeQuery(id+"F0.imprint","IMPRINT",FACE,{"disambiguationData":[TD([[makeQuery(id+"F0.imprint","IMPRINT",EDGE,{"derivedFrom":sQuery(id+"F0.wireOp",EDGE,"E231.MirrorCS")}),1.0]])]});
            var Q19;
            Q19=makeQuery(id+"F0.imprint","IMPRINT",FACE,{"disambiguationData":[TD([[makeQuery(id+"F0.imprint","IMPRINT",EDGE,{"derivedFrom":sQuery(id+"F0.wireOp",EDGE,"E239.MirrorCS")}),1.0]])]});
            var Q20;
            Q20=makeQuery(id+"F0.imprint","IMPRINT",FACE,{"disambiguationData":[TD([[makeQuery(id+"F0.imprint","IMPRINT",EDGE,{"derivedFrom":sQuery(id+"F0.wireOp",EDGE,"E235.MirrorCS")}),-1.0]])]});
            var Q21;
            Q21=makeQuery(id+"F0.imprint","IMPRINT",FACE,{"disambiguationData":[TD([[makeQuery(id+"F0.imprint","IMPRINT",EDGE,{"derivedFrom":sQuery(id+"F0.wireOp",EDGE,"E247.MirrorCS")}),-1.0]])]});
            var Q22;
            Q22=makeQuery(id+"F0.imprint","IMPRINT",FACE,{"disambiguationData":[TD([[makeQuery(id+"F0.imprint","IMPRINT",EDGE,{"derivedFrom":sQuery(id+"F0.wireOp",EDGE,"E243.MirrorCS")}),-1.0]])]});
            var Q23;
            Q23=makeQuery(id+"F0.imprint","IMPRINT",FACE,{"disambiguationData":[TD([[makeQuery(id+"F0.imprint","IMPRINT",EDGE,{"derivedFrom":sQuery(id+"F0.wireOp",EDGE,"E254.MirrorCS")}),1.0]])]});
            var Q24;
            Q24=makeQuery(id+"F0.imprint","IMPRINT",FACE,{"disambiguationData":[TD([[makeQuery(id+"F0.imprint","IMPRINT",EDGE,{"derivedFrom":sQuery(id+"F0.wireOp",EDGE,"E251.MirrorCS")}),-1.0]])]});
            var Q25;
            Q25=makeQuery(id+"F0.imprint","IMPRINT",FACE,{"disambiguationData":[TD([[makeQuery(id+"F0.imprint","IMPRINT",EDGE,{"derivedFrom":sQuery(id+"F0.wireOp",EDGE,"E259.0")}),1.0]])]});
            var Q26;
            Q26=makeQuery(id+"F0.imprint","IMPRINT",FACE,{"disambiguationData":[TD([[makeQuery(id+"F0.imprint","IMPRINT",EDGE,{"derivedFrom":sQuery(id+"F0.wireOp",EDGE,"E260.MirrorCS")}),1.0]])]});
            var Q27;
            Q27=makeQuery(id+"F0.imprint","IMPRINT",FACE,{"disambiguationData":[TD([[makeQuery(id+"F0.imprint","IMPRINT",EDGE,{"derivedFrom":sQuery(id+"F0.wireOp",EDGE,"E268.MirrorCS")}),-1.0]])]});
            var Q28;
            Q28=makeQuery(id+"F0.imprint","IMPRINT",FACE,{"disambiguationData":[TD([[makeQuery(id+"F0.imprint","IMPRINT",EDGE,{"derivedFrom":sQuery(id+"F0.wireOp",EDGE,"E264.MirrorCS")}),1.0]])]});
            var Q29;
            Q29=makeQuery(id+"F0.imprint","IMPRINT",FACE,{"disambiguationData":[TD([[makeQuery(id+"F0.imprint","IMPRINT",EDGE,{"derivedFrom":sQuery(id+"F0.wireOp",EDGE,"E281.MirrorCS")}),-1.0]])]});
            var Q30;
            Q30=makeQuery(id+"F0.imprint","IMPRINT",FACE,{"disambiguationData":[TD([[makeQuery(id+"F0.imprint","IMPRINT",EDGE,{"derivedFrom":sQuery(id+"F0.wireOp",EDGE,"E278.MirrorCS")}),-1.0]])]});
            var Q31;
            Q31=makeQuery(id+"F0.imprint","IMPRINT",FACE,{"disambiguationData":[TD([[makeQuery(id+"F0.imprint","IMPRINT",EDGE,{"derivedFrom":sQuery(id+"F0.wireOp",EDGE,"E272.MirrorCS")}),1.0]])]});
            var Q32;
            Q32=makeQuery(id+"F0.imprint","IMPRINT",FACE,{"disambiguationData":[TD([[makeQuery(id+"F0.imprint","IMPRINT",EDGE,{"derivedFrom":sQuery(id+"F0.wireOp",EDGE,"E275.MirrorCS")}),-1.0]])]});
            extrude(context, id + "F22", {"entities" : qUnion([Q0, Q1, Q2, Q3, Q4, Q5, Q6, Q7, Q8, Q9, Q10, Q11, Q12, Q13, Q14, Q15, Q16, Q17, Q18, Q19, Q20, Q21, Q22, Q23, Q24, Q25, Q26, Q27, Q28, Q29, Q30, Q31, Q32]), "depth" : 1.27 * mm});
        }
        {
            var Q0;
            {var subQ2=sQuery(id+"F0.wireOp",EDGE,"E16");Q0=makeQuery(id+"F0.imprint","IMPRINT",FACE,{"disambiguationData":[TD([[makeQuery(id+"F0.imprint","IMPRINT",EDGE,{"derivedFrom":subQ2}),1.0]])]});}
            var Q1;
            Q1=makeQuery(id+"F0.imprint","IMPRINT",FACE,{"disambiguationData":[TD([[makeQuery(id+"F0.imprint","IMPRINT",EDGE,{"derivedFrom":sQuery(id+"F0.wireOp",EDGE,"E18")}),-1.0]])]});
            var Q2;
            {var subQ2=sQuery(id+"F0.wireOp",EDGE,"E19");Q2=makeQuery(id+"F0.imprint","IMPRINT",FACE,{"disambiguationData":[TD([[makeQuery(id+"F0.imprint","IMPRINT",EDGE,{"derivedFrom":subQ2}),-1.0]])]});}
            var Q3;
            Q3=makeQuery(id+"F0.imprint","IMPRINT",FACE,{"disambiguationData":[TD([[makeQuery(id+"F0.imprint","IMPRINT",EDGE,{"derivedFrom":sQuery(id+"F0.wireOp",EDGE,"E17")}),1.0]])]});
            var Q4;
            {var subQ1=sQuery(id+"F0.wireOp",EDGE,"E97.MirrorCS");Q4=makeQuery(id+"F0.imprint","IMPRINT",FACE,{"disambiguationData":[TD([[makeQuery(id+"F0.imprint","IMPRINT",EDGE,{"derivedFrom":subQ1}),-1.0]])]});}
            var Q5;
            Q5=makeQuery(id+"F0.imprint","IMPRINT",FACE,{"disambiguationData":[TD([[makeQuery(id+"F0.imprint","IMPRINT",EDGE,{"derivedFrom":sQuery(id+"F0.wireOp",EDGE,"E141.MirrorCS")}),1.0]])]});
            var Q6;
            {var subQ1=sQuery(id+"F0.wireOp",EDGE,"E98.MirrorCS");Q6=makeQuery(id+"F0.imprint","IMPRINT",FACE,{"disambiguationData":[TD([[makeQuery(id+"F0.imprint","IMPRINT",EDGE,{"derivedFrom":subQ1}),-1.0]])]});}
            var Q7;
            Q7=makeQuery(id+"F0.imprint","IMPRINT",FACE,{"disambiguationData":[TD([[makeQuery(id+"F0.imprint","IMPRINT",EDGE,{"derivedFrom":sQuery(id+"F0.wireOp",EDGE,"E170.MirrorCS")}),1.0]])]});
            extrude(context, id + "F23", {"entities" : qUnion([Q0, Q1, Q2, Q3, Q4, Q5, Q6, Q7]), "depth" : 1.27 * mm});
        }
        {
            var Q0;
            Q0=makeQuery(id+"F0.imprint","IMPRINT",FACE,{"disambiguationData":[TD([[makeQuery(id+"F0.imprint","IMPRINT",EDGE,{"derivedFrom":sQuery(id+"F0.wireOp",EDGE,"E17")}),-1.0]])]});
            var Q1;
            Q1=makeQuery(id+"F0.imprint","IMPRINT",FACE,{"disambiguationData":[TD([[makeQuery(id+"F0.imprint","IMPRINT",EDGE,{"derivedFrom":sQuery(id+"F0.wireOp",EDGE,"E18")}),1.0]])]});
            var Q2;
            {var subQ1=sQuery(id+"F0.wireOp",EDGE,"E19");Q2=makeQuery(id+"F0.imprint","IMPRINT",FACE,{"disambiguationData":[TD([[makeQuery(id+"F0.imprint","IMPRINT",EDGE,{"derivedFrom":subQ1}),1.0]])]});}
            var Q3;
            {var subQ2=sQuery(id+"F0.wireOp",EDGE,"E16");Q3=makeQuery(id+"F0.imprint","IMPRINT",FACE,{"disambiguationData":[TD([[makeQuery(id+"F0.imprint","IMPRINT",EDGE,{"derivedFrom":subQ2}),-1.0]])]});}
            var Q4;
            {var subQ2=sQuery(id+"F0.wireOp",EDGE,"E97.MirrorCS");Q4=makeQuery(id+"F0.imprint","IMPRINT",FACE,{"disambiguationData":[TD([[makeQuery(id+"F0.imprint","IMPRINT",EDGE,{"derivedFrom":subQ2}),1.0]])]});}
            var Q5;
            Q5=makeQuery(id+"F0.imprint","IMPRINT",FACE,{"disambiguationData":[TD([[makeQuery(id+"F0.imprint","IMPRINT",EDGE,{"derivedFrom":sQuery(id+"F0.wireOp",EDGE,"E170.MirrorCS")}),-1.0]])]});
            var Q6;
            Q6=makeQuery(id+"F0.imprint","IMPRINT",FACE,{"disambiguationData":[TD([[makeQuery(id+"F0.imprint","IMPRINT",EDGE,{"derivedFrom":sQuery(id+"F0.wireOp",EDGE,"E174.MirrorCS")}),1.0]])]});
            var Q7;
            {var subQ1=sQuery(id+"F0.wireOp",EDGE,"E98.MirrorCS");Q7=makeQuery(id+"F0.imprint","IMPRINT",FACE,{"disambiguationData":[TD([[makeQuery(id+"F0.imprint","IMPRINT",EDGE,{"derivedFrom":subQ1}),1.0]])]});}
            extrude(context, id + "F24", {"entities" : qUnion([Q0, Q1, Q2, Q3, Q4, Q5, Q6, Q7]), "depth" : 1.27 * mm});
        }
        {
            var Q0;
            Q0=makeQuery(id+"F0.imprint","IMPRINT",FACE,{"disambiguationData":[TD([[makeQuery(id+"F0.imprint","IMPRINT",EDGE,{"derivedFrom":sQuery(id+"F0.wireOp",EDGE,"E208.MirrorCS")}),-1.0]])]});
            var Q1;
            Q1=makeQuery(id+"F0.imprint","IMPRINT",FACE,{"disambiguationData":[TD([[makeQuery(id+"F0.imprint","IMPRINT",EDGE,{"derivedFrom":sQuery(id+"F0.wireOp",EDGE,"84fd1f12-c4b3-46c8-b99e-ff9fed08b64b0.MirrorCS")}),1.0]])]});
            var Q2;
            Q2=makeQuery(id+"F0.imprint","IMPRINT",FACE,{"disambiguationData":[TD([[makeQuery(id+"F0.imprint","IMPRINT",EDGE,{"derivedFrom":sQuery(id+"F0.wireOp",EDGE,"E210.MirrorCS")}),-1.0]])]});
            var Q3;
            Q3=makeQuery(id+"F0.imprint","IMPRINT",FACE,{"disambiguationData":[TD([[makeQuery(id+"F0.imprint","IMPRINT",EDGE,{"derivedFrom":sQuery(id+"F0.wireOp",EDGE,"E199.MirrorCS")}),-1.0]])]});
            var Q4;
            Q4=makeQuery(id+"F0.imprint","IMPRINT",FACE,{"disambiguationData":[TD([[makeQuery(id+"F0.imprint","IMPRINT",EDGE,{"derivedFrom":sQuery(id+"F0.wireOp",EDGE,"E197")}),1.0]])]});
            var Q5;
            Q5=makeQuery(id+"F0.imprint","IMPRINT",FACE,{"disambiguationData":[TD([[makeQuery(id+"F0.imprint","IMPRINT",EDGE,{"derivedFrom":sQuery(id+"F0.wireOp",EDGE,"E204")}),1.0]])]});
            var Q6;
            Q6=makeQuery(id+"F0.imprint","IMPRINT",FACE,{"disambiguationData":[TD([[makeQuery(id+"F0.imprint","IMPRINT",EDGE,{"derivedFrom":sQuery(id+"F0.wireOp",EDGE,"E202.MirrorCS")}),-1.0]])]});
            var Q7;
            Q7=makeQuery(id+"F0.imprint","IMPRINT",FACE,{"disambiguationData":[TD([[makeQuery(id+"F0.imprint","IMPRINT",EDGE,{"derivedFrom":sQuery(id+"F0.wireOp",EDGE,"E206")}),1.0]])]});
            var Q8;
            Q8=makeQuery(id+"F0.imprint","IMPRINT",FACE,{"disambiguationData":[TD([[makeQuery(id+"F0.imprint","IMPRINT",EDGE,{"derivedFrom":sQuery(id+"F0.wireOp",EDGE,"E201.MirrorCS")}),1.0]])]});
            extrude(context, id + "F25", {"entities" : qUnion([Q0, Q1, Q2, Q3, Q4, Q5, Q6, Q7, Q8]), "depth" : 1.27 * mm});
        }
        {
            var Q0;
            Q0=makeQuery(id+"F25.opExtrude","CAP_FACE",FACE,{"disambiguationData":[OSD([sQuery(id+"F0.wireOp",EDGE,"E208.MirrorCS"),sQuery(id+"F0.wireOp",EDGE,"E209.MirrorCS"),sQuery(id+"F0.wireOp",EDGE,"E212.0"),sQuery(id+"F0.wireOp",EDGE,"E212.1")])],"isStart":false});
            var Q1;
            Q1=makeQuery(id+"F25.opExtrude","CAP_FACE",FACE,{"disambiguationData":[OSD([sQuery(id+"F0.wireOp",EDGE,"84fd1f12-c4b3-46c8-b99e-ff9fed08b64b0.MirrorCS"),sQuery(id+"F0.wireOp",EDGE,"E201.MirrorCS"),sQuery(id+"F0.wireOp",EDGE,"E215.0"),sQuery(id+"F0.wireOp",EDGE,"E215.1")])],"isStart":false});
            var Q2;
            Q2=makeQuery(id+"F25.opExtrude","CAP_FACE",FACE,{"disambiguationData":[OSD([sQuery(id+"F0.wireOp",EDGE,"E199.MirrorCS"),sQuery(id+"F0.wireOp",EDGE,"E200.MirrorCS"),sQuery(id+"F0.wireOp",EDGE,"E214.0"),sQuery(id+"F0.wireOp",EDGE,"E214.1")])],"isStart":false});
            var Q3;
            Q3=makeQuery(id+"F25.opExtrude","CAP_FACE",FACE,{"disambiguationData":[OSD([sQuery(id+"F0.wireOp",EDGE,"E197"),sQuery(id+"F0.wireOp",EDGE,"E198"),sQuery(id+"F0.wireOp",EDGE,"E222.MirrorCS"),sQuery(id+"F0.wireOp",EDGE,"E223.MirrorCS")])],"isStart":false});
            var Q4;
            Q4=makeQuery(id+"F25.opExtrude","CAP_FACE",FACE,{"disambiguationData":[OSD([sQuery(id+"F0.wireOp",EDGE,"E204"),sQuery(id+"F0.wireOp",EDGE,"E205"),sQuery(id+"F0.wireOp",EDGE,"E220.MirrorCS"),sQuery(id+"F0.wireOp",EDGE,"E221.MirrorCS")])],"isStart":false});
            var Q5;
            Q5=makeQuery(id+"F25.opExtrude","CAP_FACE",FACE,{"disambiguationData":[OSD([sQuery(id+"F0.wireOp",EDGE,"E206"),sQuery(id+"F0.wireOp",EDGE,"E207"),sQuery(id+"F0.wireOp",EDGE,"E218.MirrorCS"),sQuery(id+"F0.wireOp",EDGE,"E219.MirrorCS")])],"isStart":false});
            var Q6;
            Q6=makeQuery(id+"F25.opExtrude","CAP_FACE",FACE,{"disambiguationData":[OSD([sQuery(id+"F0.wireOp",EDGE,"E202.MirrorCS"),sQuery(id+"F0.wireOp",EDGE,"E203.MirrorCS"),sQuery(id+"F0.wireOp",EDGE,"E216.MirrorCS"),sQuery(id+"F0.wireOp",EDGE,"E217.MirrorCS")])],"isStart":false});
            var Q7;
            Q7=makeQuery(id+"F25.opExtrude","CAP_FACE",FACE,{"disambiguationData":[OSD([sQuery(id+"F0.wireOp",EDGE,"E210.MirrorCS"),sQuery(id+"F0.wireOp",EDGE,"E211.MirrorCS"),sQuery(id+"F0.wireOp",EDGE,"E213.0"),sQuery(id+"F0.wireOp",EDGE,"E213.1")])],"isStart":false});
            var Q8;
            Q8=makeQuery(id+"F22.opExtrude","CAP_FACE",FACE,{"disambiguationData":[OSD([sQuery(id+"F0.wireOp",EDGE,"E231.MirrorCS"),sQuery(id+"F0.wireOp",EDGE,"E232.MirrorCS"),sQuery(id+"F0.wireOp",EDGE,"E233.MirrorCS"),sQuery(id+"F0.wireOp",EDGE,"E234.MirrorCS")])],"isStart":false});
            var Q9;
            Q9=makeQuery(id+"F22.opExtrude","CAP_FACE",FACE,{"disambiguationData":[OSD([sQuery(id+"F0.wireOp",EDGE,"E259.0"),sQuery(id+"F0.wireOp",EDGE,"E259.1"),sQuery(id+"F0.wireOp",EDGE,"E259.2"),sQuery(id+"F0.wireOp",EDGE,"E259.3")])],"isStart":false});
            var Q10;
            Q10=makeQuery(id+"F22.opExtrude","CAP_FACE",FACE,{"disambiguationData":[OSD([sQuery(id+"F0.wireOp",EDGE,"E230.0"),sQuery(id+"F0.wireOp",EDGE,"E230.1"),sQuery(id+"F0.wireOp",EDGE,"E230.2"),sQuery(id+"F0.wireOp",EDGE,"E230.3")])],"isStart":false});
            var Q11;
            Q11=makeQuery(id+"F22.opExtrude","CAP_FACE",FACE,{"disambiguationData":[OSD([sQuery(id+"F0.wireOp",EDGE,"E264.MirrorCS"),sQuery(id+"F0.wireOp",EDGE,"E265.MirrorCS"),sQuery(id+"F0.wireOp",EDGE,"E266.MirrorCS"),sQuery(id+"F0.wireOp",EDGE,"E267.MirrorCS")])],"isStart":false});
            var Q12;
            Q12=makeQuery(id+"F22.opExtrude","CAP_FACE",FACE,{"disambiguationData":[OSD([sQuery(id+"F0.wireOp",EDGE,"E268.MirrorCS"),sQuery(id+"F0.wireOp",EDGE,"E269.MirrorCS"),sQuery(id+"F0.wireOp",EDGE,"E270.MirrorCS"),sQuery(id+"F0.wireOp",EDGE,"E271.MirrorCS")])],"isStart":false});
            var Q13;
            Q13=makeQuery(id+"F22.opExtrude","CAP_FACE",FACE,{"disambiguationData":[OSD([sQuery(id+"F0.wireOp",EDGE,"E239.MirrorCS"),sQuery(id+"F0.wireOp",EDGE,"E240.MirrorCS"),sQuery(id+"F0.wireOp",EDGE,"E241.MirrorCS"),sQuery(id+"F0.wireOp",EDGE,"E242.MirrorCS")])],"isStart":false});
            var Q14;
            Q14=makeQuery(id+"F22.opExtrude","CAP_FACE",FACE,{"disambiguationData":[OSD([sQuery(id+"F0.wireOp",EDGE,"E235.MirrorCS"),sQuery(id+"F0.wireOp",EDGE,"E236.MirrorCS"),sQuery(id+"F0.wireOp",EDGE,"E237.MirrorCS"),sQuery(id+"F0.wireOp",EDGE,"E238.MirrorCS")])],"isStart":false});
            var Q15;
            Q15=makeQuery(id+"F22.opExtrude","CAP_FACE",FACE,{"disambiguationData":[OSD([sQuery(id+"F0.wireOp",EDGE,"E260.MirrorCS"),sQuery(id+"F0.wireOp",EDGE,"E261.MirrorCS"),sQuery(id+"F0.wireOp",EDGE,"E262.MirrorCS"),sQuery(id+"F0.wireOp",EDGE,"E263.MirrorCS")])],"isStart":false});
            var Q16;
            Q16=makeQuery(id+"F22.opExtrude","CAP_FACE",FACE,{"disambiguationData":[OSD([sQuery(id+"F0.wireOp",EDGE,"E243.MirrorCS"),sQuery(id+"F0.wireOp",EDGE,"E244.MirrorCS"),sQuery(id+"F0.wireOp",EDGE,"E245.MirrorCS"),sQuery(id+"F0.wireOp",EDGE,"E246.MirrorCS")])],"isStart":false});
            var Q17;
            Q17=makeQuery(id+"F22.opExtrude","CAP_FACE",FACE,{"disambiguationData":[OSD([sQuery(id+"F0.wireOp",EDGE,"E247.MirrorCS"),sQuery(id+"F0.wireOp",EDGE,"E248.MirrorCS"),sQuery(id+"F0.wireOp",EDGE,"E249.MirrorCS"),sQuery(id+"F0.wireOp",EDGE,"E250.MirrorCS")])],"isStart":false});
            var Q18;
            Q18=makeQuery(id+"F22.opExtrude","CAP_FACE",FACE,{"disambiguationData":[OSD([sQuery(id+"F0.wireOp",EDGE,"E281.MirrorCS"),sQuery(id+"F0.wireOp",EDGE,"E282.MirrorCS"),sQuery(id+"F0.wireOp",EDGE,"E284.MirrorCS"),sQuery(id+"F0.wireOp",EDGE,"E287.MirrorCS")])],"isStart":false});
            var Q19;
            Q19=makeQuery(id+"F22.opExtrude","CAP_FACE",FACE,{"disambiguationData":[OSD([sQuery(id+"F0.wireOp",EDGE,"E272.MirrorCS"),sQuery(id+"F0.wireOp",EDGE,"E273.MirrorCS"),sQuery(id+"F0.wireOp",EDGE,"E274.MirrorCS"),sQuery(id+"F0.wireOp",EDGE,"E286.MirrorCS")])],"isStart":false});
            var Q20;
            Q20=makeQuery(id+"F22.opExtrude","CAP_FACE",FACE,{"disambiguationData":[OSD([sQuery(id+"F0.wireOp",EDGE,"E278.MirrorCS"),sQuery(id+"F0.wireOp",EDGE,"E279.MirrorCS"),sQuery(id+"F0.wireOp",EDGE,"E280.MirrorCS"),sQuery(id+"F0.wireOp",EDGE,"E283.MirrorCS")])],"isStart":false});
            var Q21;
            Q21=makeQuery(id+"F22.opExtrude","CAP_FACE",FACE,{"disambiguationData":[OSD([sQuery(id+"F0.wireOp",EDGE,"E275.MirrorCS"),sQuery(id+"F0.wireOp",EDGE,"E276.MirrorCS"),sQuery(id+"F0.wireOp",EDGE,"E277.MirrorCS"),sQuery(id+"F0.wireOp",EDGE,"E285.MirrorCS")])],"isStart":false});
            var Q22;
            Q22=makeQuery(id+"F22.opExtrude","CAP_FACE",FACE,{"disambiguationData":[OSD([sQuery(id+"F0.wireOp",EDGE,"E254.MirrorCS"),sQuery(id+"F0.wireOp",EDGE,"E255.MirrorCS"),sQuery(id+"F0.wireOp",EDGE,"E256.MirrorCS"),sQuery(id+"F0.wireOp",EDGE,"E257.MirrorCS")])],"isStart":false});
            var Q23;
            Q23=makeQuery(id+"F22.opExtrude","CAP_FACE",FACE,{"disambiguationData":[OSD([sQuery(id+"F0.wireOp",EDGE,"E251.MirrorCS"),sQuery(id+"F0.wireOp",EDGE,"E252.MirrorCS"),sQuery(id+"F0.wireOp",EDGE,"E253.MirrorCS"),sQuery(id+"F0.wireOp",EDGE,"E258.MirrorCS")])],"isStart":false});
            fillet(context, id + "F26", {"entities" : qUnion([Q0, Q1, Q2, Q3, Q4, Q5, Q6, Q7, Q8, Q9, Q10, Q11, Q12, Q13, Q14, Q15, Q16, Q17, Q18, Q19, Q20, Q21, Q22, Q23]), "radius" : 0.5 * mm, "tangentPropagation" : true, "allowEdgeOverflow" : false});
        }
        {
            var Q0;
            Q0=makeQuery(id+"F24.opExtrude","CAP_FACE",FACE,{"disambiguationData":[OSD([sQuery(id+"F0.wireOp",EDGE,"E17"),sQuery(id+"F0.wireOp",EDGE,"E67"),sQuery(id+"F0.wireOp",EDGE,"E211.MirrorCS"),sQuery(id+"F0.wireOp",EDGE,"E224"),sQuery(id+"F0.wireOp",EDGE,"E259.0"),sQuery(id+"F0.wireOp",EDGE,"E259.1"),sQuery(id+"F0.wireOp",EDGE,"E259.2"),sQuery(id+"F0.wireOp",EDGE,"E259.3")])],"isStart":false});
            var Q1;
            Q1=makeQuery(id+"F23.opExtrude","CAP_FACE",FACE,{"disambiguationData":[OSD([sQuery(id+"F0.wireOp",EDGE,"E17"),sQuery(id+"F0.wireOp",EDGE,"E66"),sQuery(id+"F0.wireOp",EDGE,"E200.MirrorCS"),sQuery(id+"F0.wireOp",EDGE,"E225"),sQuery(id+"F0.wireOp",EDGE,"E260.MirrorCS"),sQuery(id+"F0.wireOp",EDGE,"E261.MirrorCS"),sQuery(id+"F0.wireOp",EDGE,"E262.MirrorCS"),sQuery(id+"F0.wireOp",EDGE,"E263.MirrorCS")])],"isStart":false});
            var Q2;
            Q2=makeQuery(id+"F23.opExtrude","CAP_FACE",FACE,{"disambiguationData":[OSD([sQuery(id+"F0.wireOp",EDGE,"E6"),sQuery(id+"F0.wireOp",EDGE,"E19"),sQuery(id+"F0.wireOp",EDGE,"E65"),sQuery(id+"F0.wireOp",EDGE,"E199.MirrorCS"),sQuery(id+"F0.wireOp",EDGE,"E235.MirrorCS"),sQuery(id+"F0.wireOp",EDGE,"E236.MirrorCS"),sQuery(id+"F0.wireOp",EDGE,"E237.MirrorCS"),sQuery(id+"F0.wireOp",EDGE,"E238.MirrorCS")])],"isStart":false});
            var Q3;
            Q3=makeQuery(id+"F24.opExtrude","CAP_FACE",FACE,{"disambiguationData":[OSD([sQuery(id+"F0.wireOp",EDGE,"E6"),sQuery(id+"F0.wireOp",EDGE,"E97.MirrorCS"),sQuery(id+"F0.wireOp",EDGE,"E153.MirrorCS"),sQuery(id+"F0.wireOp",EDGE,"E197"),sQuery(id+"F0.wireOp",EDGE,"E247.MirrorCS"),sQuery(id+"F0.wireOp",EDGE,"E248.MirrorCS"),sQuery(id+"F0.wireOp",EDGE,"E249.MirrorCS"),sQuery(id+"F0.wireOp",EDGE,"E250.MirrorCS")])],"isStart":false});
            var Q4;
            Q4=makeQuery(id+"F24.opExtrude","CAP_FACE",FACE,{"disambiguationData":[OSD([sQuery(id+"F0.wireOp",EDGE,"E170.MirrorCS"),sQuery(id+"F0.wireOp",EDGE,"E185.MirrorCS"),sQuery(id+"F0.wireOp",EDGE,"E198"),sQuery(id+"F0.wireOp",EDGE,"E226"),sQuery(id+"F0.wireOp",EDGE,"E272.MirrorCS"),sQuery(id+"F0.wireOp",EDGE,"E273.MirrorCS"),sQuery(id+"F0.wireOp",EDGE,"E274.MirrorCS"),sQuery(id+"F0.wireOp",EDGE,"E286.MirrorCS")])],"isStart":false});
            var Q5;
            Q5=makeQuery(id+"F23.opExtrude","CAP_FACE",FACE,{"disambiguationData":[OSD([sQuery(id+"F0.wireOp",EDGE,"E170.MirrorCS"),sQuery(id+"F0.wireOp",EDGE,"E180.MirrorCS"),sQuery(id+"F0.wireOp",EDGE,"E204"),sQuery(id+"F0.wireOp",EDGE,"E227"),sQuery(id+"F0.wireOp",EDGE,"E275.MirrorCS"),sQuery(id+"F0.wireOp",EDGE,"E276.MirrorCS"),sQuery(id+"F0.wireOp",EDGE,"E277.MirrorCS"),sQuery(id+"F0.wireOp",EDGE,"E285.MirrorCS")])],"isStart":false});
            var Q6;
            Q6=makeQuery(id+"F23.opExtrude","CAP_FACE",FACE,{"disambiguationData":[OSD([sQuery(id+"F0.wireOp",EDGE,"E45"),sQuery(id+"F0.wireOp",EDGE,"E98.MirrorCS"),sQuery(id+"F0.wireOp",EDGE,"E189.MirrorCS"),sQuery(id+"F0.wireOp",EDGE,"E205"),sQuery(id+"F0.wireOp",EDGE,"E254.MirrorCS"),sQuery(id+"F0.wireOp",EDGE,"E255.MirrorCS"),sQuery(id+"F0.wireOp",EDGE,"E256.MirrorCS"),sQuery(id+"F0.wireOp",EDGE,"E257.MirrorCS")])],"isStart":false});
            var Q7;
            Q7=makeQuery(id+"F24.opExtrude","CAP_FACE",FACE,{"disambiguationData":[OSD([sQuery(id+"F0.wireOp",EDGE,"E18"),sQuery(id+"F0.wireOp",EDGE,"E68"),sQuery(id+"F0.wireOp",EDGE,"E210.MirrorCS"),sQuery(id+"F0.wireOp",EDGE,"E229"),sQuery(id+"F0.wireOp",EDGE,"E231.MirrorCS"),sQuery(id+"F0.wireOp",EDGE,"E232.MirrorCS"),sQuery(id+"F0.wireOp",EDGE,"E233.MirrorCS"),sQuery(id+"F0.wireOp",EDGE,"E234.MirrorCS")])],"isStart":false});
            var Q8;
            Q8=makeQuery(id+"F24.opExtrude","CAP_FACE",FACE,{"disambiguationData":[OSD([sQuery(id+"F0.wireOp",EDGE,"E45"),sQuery(id+"F0.wireOp",EDGE,"E98.MirrorCS"),sQuery(id+"F0.wireOp",EDGE,"E167.MirrorCS"),sQuery(id+"F0.wireOp",EDGE,"E207"),sQuery(id+"F0.wireOp",EDGE,"E251.MirrorCS"),sQuery(id+"F0.wireOp",EDGE,"E252.MirrorCS"),sQuery(id+"F0.wireOp",EDGE,"E253.MirrorCS"),sQuery(id+"F0.wireOp",EDGE,"E258.MirrorCS")])],"isStart":false});
            var Q9;
            Q9=makeQuery(id+"F24.opExtrude","CAP_FACE",FACE,{"disambiguationData":[OSD([sQuery(id+"F0.wireOp",EDGE,"E53"),sQuery(id+"F0.wireOp",EDGE,"E174.MirrorCS"),sQuery(id+"F0.wireOp",EDGE,"E182.MirrorCS"),sQuery(id+"F0.wireOp",EDGE,"E206"),sQuery(id+"F0.wireOp",EDGE,"E278.MirrorCS"),sQuery(id+"F0.wireOp",EDGE,"E279.MirrorCS"),sQuery(id+"F0.wireOp",EDGE,"E280.MirrorCS"),sQuery(id+"F0.wireOp",EDGE,"E283.MirrorCS")])],"isStart":false});
            var Q10;
            Q10=makeQuery(id+"F23.opExtrude","CAP_FACE",FACE,{"disambiguationData":[OSD([sQuery(id+"F0.wireOp",EDGE,"E53"),sQuery(id+"F0.wireOp",EDGE,"E141.MirrorCS"),sQuery(id+"F0.wireOp",EDGE,"E182.MirrorCS"),sQuery(id+"F0.wireOp",EDGE,"E203.MirrorCS"),sQuery(id+"F0.wireOp",EDGE,"E281.MirrorCS"),sQuery(id+"F0.wireOp",EDGE,"E282.MirrorCS"),sQuery(id+"F0.wireOp",EDGE,"E284.MirrorCS"),sQuery(id+"F0.wireOp",EDGE,"E287.MirrorCS")])],"isStart":false});
            var Q11;
            Q11=makeQuery(id+"F23.opExtrude","CAP_FACE",FACE,{"disambiguationData":[OSD([sQuery(id+"F0.wireOp",EDGE,"E6"),sQuery(id+"F0.wireOp",EDGE,"E97.MirrorCS"),sQuery(id+"F0.wireOp",EDGE,"E148.MirrorCS"),sQuery(id+"F0.wireOp",EDGE,"E202.MirrorCS"),sQuery(id+"F0.wireOp",EDGE,"E243.MirrorCS"),sQuery(id+"F0.wireOp",EDGE,"E244.MirrorCS"),sQuery(id+"F0.wireOp",EDGE,"E245.MirrorCS"),sQuery(id+"F0.wireOp",EDGE,"E246.MirrorCS")])],"isStart":false});
            var Q12;
            Q12=makeQuery(id+"F24.opExtrude","CAP_FACE",FACE,{"disambiguationData":[OSD([sQuery(id+"F0.wireOp",EDGE,"E16"),sQuery(id+"F0.wireOp",EDGE,"E53"),sQuery(id+"F0.wireOp",EDGE,"E71"),sQuery(id+"F0.wireOp",EDGE,"E201.MirrorCS"),sQuery(id+"F0.wireOp",EDGE,"E268.MirrorCS"),sQuery(id+"F0.wireOp",EDGE,"E269.MirrorCS"),sQuery(id+"F0.wireOp",EDGE,"E270.MirrorCS"),sQuery(id+"F0.wireOp",EDGE,"E271.MirrorCS")])],"isStart":false});
            var Q13;
            Q13=makeQuery(id+"F23.opExtrude","CAP_FACE",FACE,{"disambiguationData":[OSD([sQuery(id+"F0.wireOp",EDGE,"E16"),sQuery(id+"F0.wireOp",EDGE,"E53"),sQuery(id+"F0.wireOp",EDGE,"E70"),sQuery(id+"F0.wireOp",EDGE,"E208.MirrorCS"),sQuery(id+"F0.wireOp",EDGE,"E264.MirrorCS"),sQuery(id+"F0.wireOp",EDGE,"E265.MirrorCS"),sQuery(id+"F0.wireOp",EDGE,"E266.MirrorCS"),sQuery(id+"F0.wireOp",EDGE,"E267.MirrorCS")])],"isStart":false});
            var Q14;
            Q14=makeQuery(id+"F23.opExtrude","CAP_FACE",FACE,{"disambiguationData":[OSD([sQuery(id+"F0.wireOp",EDGE,"E18"),sQuery(id+"F0.wireOp",EDGE,"E69"),sQuery(id+"F0.wireOp",EDGE,"E209.MirrorCS"),sQuery(id+"F0.wireOp",EDGE,"E228"),sQuery(id+"F0.wireOp",EDGE,"E230.0"),sQuery(id+"F0.wireOp",EDGE,"E230.1"),sQuery(id+"F0.wireOp",EDGE,"E230.2"),sQuery(id+"F0.wireOp",EDGE,"E230.3")])],"isStart":false});
            var Q15;
            Q15=makeQuery(id+"F24.opExtrude","CAP_EDGE",EDGE,{"disambiguationData":[OSD([sQuery(id+"F0.wireOp",EDGE,"E64")])],"isStart":false});
            var Q16;
            Q16=makeQuery(id+"F24.opExtrude","CAP_EDGE",EDGE,{"disambiguationData":[OSD([sQuery(id+"F0.wireOp",EDGE,"E19")])],"isStart":false});
            var Q17;
            {var subQ0=sQuery(id+"F0.wireOp",EDGE,"E6");Q17=makeQuery(id+"F24.opExtrude","CAP_EDGE",EDGE,{"disambiguationData":[OSD([subQ0]),TDD([makeQuery(id+"F0.imprint","IMPRINT",EDGE,{"disambiguationData":[TD([[makeQuery(id+"F0.imprint","INTERSECT",VERTEX,{"derivedFrom":[subQ0,sQuery(id+"F0.wireOp",EDGE,"E19"),sQuery(id+"F0.wireOp",EDGE,"E97.MirrorCS")]}),-1.0]])],"derivedFrom":subQ0})])],"isStart":false});}
            var Q18;
            Q18=makeQuery(id+"F24.opExtrude","CAP_EDGE",EDGE,{"disambiguationData":[OSD([sQuery(id+"F0.wireOp",EDGE,"E241.MirrorCS")])],"isStart":false});
            var Q19;
            Q19=makeQuery(id+"F24.opExtrude","CAP_EDGE",EDGE,{"disambiguationData":[OSD([sQuery(id+"F0.wireOp",EDGE,"E242.MirrorCS")])],"isStart":false});
            var Q20;
            Q20=makeQuery(id+"F24.opExtrude","CAP_EDGE",EDGE,{"disambiguationData":[OSD([sQuery(id+"F0.wireOp",EDGE,"E240.MirrorCS")])],"isStart":false});
            var Q21;
            Q21=makeQuery(id+"F24.opExtrude","CAP_EDGE",EDGE,{"disambiguationData":[OSD([sQuery(id+"F0.wireOp",EDGE,"E288")])],"isStart":false});
            fillet(context, id + "F27", {"entities" : qUnion([Q0, Q1, Q2, Q3, Q4, Q5, Q6, Q7, Q8, Q9, Q10, Q11, Q12, Q13, Q14, Q15, Q16, Q17, Q18, Q19, Q20, Q21]), "radius" : 0.5 * mm, "tangentPropagation" : true, "allowEdgeOverflow" : false});
        }
        {
            var Q0;
            Q0=makeQuery(id+"F22.opExtrude","CAP_FACE",FACE,{"disambiguationData":[OSD([sQuery(id+"F0.wireOp",EDGE,"E218.MirrorCS"),sQuery(id+"F0.wireOp",EDGE,"E219.MirrorCS")])],"isStart":false});
            var Q1;
            Q1=makeQuery(id+"F22.opExtrude","CAP_FACE",FACE,{"disambiguationData":[OSD([sQuery(id+"F0.wireOp",EDGE,"E220.MirrorCS"),sQuery(id+"F0.wireOp",EDGE,"E221.MirrorCS")])],"isStart":false});
            var Q2;
            Q2=makeQuery(id+"F22.opExtrude","CAP_FACE",FACE,{"disambiguationData":[OSD([sQuery(id+"F0.wireOp",EDGE,"E222.MirrorCS"),sQuery(id+"F0.wireOp",EDGE,"E223.MirrorCS")])],"isStart":false});
            var Q3;
            Q3=makeQuery(id+"F22.opExtrude","CAP_FACE",FACE,{"disambiguationData":[OSD([sQuery(id+"F0.wireOp",EDGE,"E214.0"),sQuery(id+"F0.wireOp",EDGE,"E214.1")])],"isStart":false});
            var Q4;
            Q4=makeQuery(id+"F22.opExtrude","CAP_FACE",FACE,{"disambiguationData":[OSD([sQuery(id+"F0.wireOp",EDGE,"E216.MirrorCS"),sQuery(id+"F0.wireOp",EDGE,"E217.MirrorCS")])],"isStart":false});
            var Q5;
            Q5=makeQuery(id+"F22.opExtrude","CAP_FACE",FACE,{"disambiguationData":[OSD([sQuery(id+"F0.wireOp",EDGE,"E215.0"),sQuery(id+"F0.wireOp",EDGE,"E215.1")])],"isStart":false});
            var Q6;
            Q6=makeQuery(id+"F22.opExtrude","CAP_FACE",FACE,{"disambiguationData":[OSD([sQuery(id+"F0.wireOp",EDGE,"E212.0"),sQuery(id+"F0.wireOp",EDGE,"E212.1")])],"isStart":false});
            var Q7;
            Q7=makeQuery(id+"F22.opExtrude","CAP_FACE",FACE,{"disambiguationData":[OSD([sQuery(id+"F0.wireOp",EDGE,"E213.0"),sQuery(id+"F0.wireOp",EDGE,"E213.1")])],"isStart":false});
            fillet(context, id + "F28", {"entities" : qUnion([Q0, Q1, Q2, Q3, Q4, Q5, Q6, Q7]), "radius" : 0.5 * mm, "tangentPropagation" : true, "allowEdgeOverflow" : false});
        }
        {
            var Q0;
            Q0=makeQuery(id+"F6.opExtrude","CAP_FACE",FACE,{"disambiguationData":[OSD([sQuery(id+"F0.wireOp",EDGE,"E88.MirrorCS"),sQuery(id+"F0.wireOp",EDGE,"E89.MirrorCS"),sQuery(id+"F0.wireOp",EDGE,"E90.MirrorCS"),sQuery(id+"F0.wireOp",EDGE,"E91.MirrorCS"),sQuery(id+"F0.wireOp",EDGE,"E92.MirrorCS"),sQuery(id+"F0.wireOp",EDGE,"E93.MirrorCS"),sQuery(id+"F0.wireOp",EDGE,"E94.MirrorCS"),sQuery(id+"F0.wireOp",EDGE,"E95.MirrorCS")])],"isStart":false});
            var Q1;
            Q1=makeQuery(id+"F6.opExtrude","CAP_FACE",FACE,{"disambiguationData":[OSD([sQuery(id+"F0.wireOp",EDGE,"E36.0"),sQuery(id+"F0.wireOp",EDGE,"E36.1"),sQuery(id+"F0.wireOp",EDGE,"E36.2"),sQuery(id+"F0.wireOp",EDGE,"E36.3"),sQuery(id+"F0.wireOp",EDGE,"E36.4"),sQuery(id+"F0.wireOp",EDGE,"E36.5"),sQuery(id+"F0.wireOp",EDGE,"E36.6"),sQuery(id+"F0.wireOp",EDGE,"E36.7")])],"isStart":false});
            extrude(context, id + "F29", {"entities" : qUnion([Q0, Q1]), "depth" : 0.22 * mm});
        }
        {
            var Q0;
            Q0=makeQuery(id+"F29.opExtrude","CAP_FACE",FACE,{"disambiguationData":[OSD([sQuery(id+"F0.wireOp",EDGE,"E88.MirrorCS"),sQuery(id+"F0.wireOp",EDGE,"E89.MirrorCS"),sQuery(id+"F0.wireOp",EDGE,"E90.MirrorCS"),sQuery(id+"F0.wireOp",EDGE,"E91.MirrorCS"),sQuery(id+"F0.wireOp",EDGE,"E92.MirrorCS"),sQuery(id+"F0.wireOp",EDGE,"E93.MirrorCS"),sQuery(id+"F0.wireOp",EDGE,"E94.MirrorCS"),sQuery(id+"F0.wireOp",EDGE,"E95.MirrorCS")])],"isStart":false});
            var Q1;
            Q1=makeQuery(id+"F29.opExtrude","CAP_FACE",FACE,{"disambiguationData":[OSD([sQuery(id+"F0.wireOp",EDGE,"E36.0"),sQuery(id+"F0.wireOp",EDGE,"E36.1"),sQuery(id+"F0.wireOp",EDGE,"E36.2"),sQuery(id+"F0.wireOp",EDGE,"E36.3"),sQuery(id+"F0.wireOp",EDGE,"E36.4"),sQuery(id+"F0.wireOp",EDGE,"E36.5"),sQuery(id+"F0.wireOp",EDGE,"E36.6"),sQuery(id+"F0.wireOp",EDGE,"E36.7")])],"isStart":false});
            fillet(context, id + "F30", {"entities" : qUnion([Q0, Q1]), "radius" : 0.22 * mm, "tangentPropagation" : true, "allowEdgeOverflow" : false});
        }
    });
